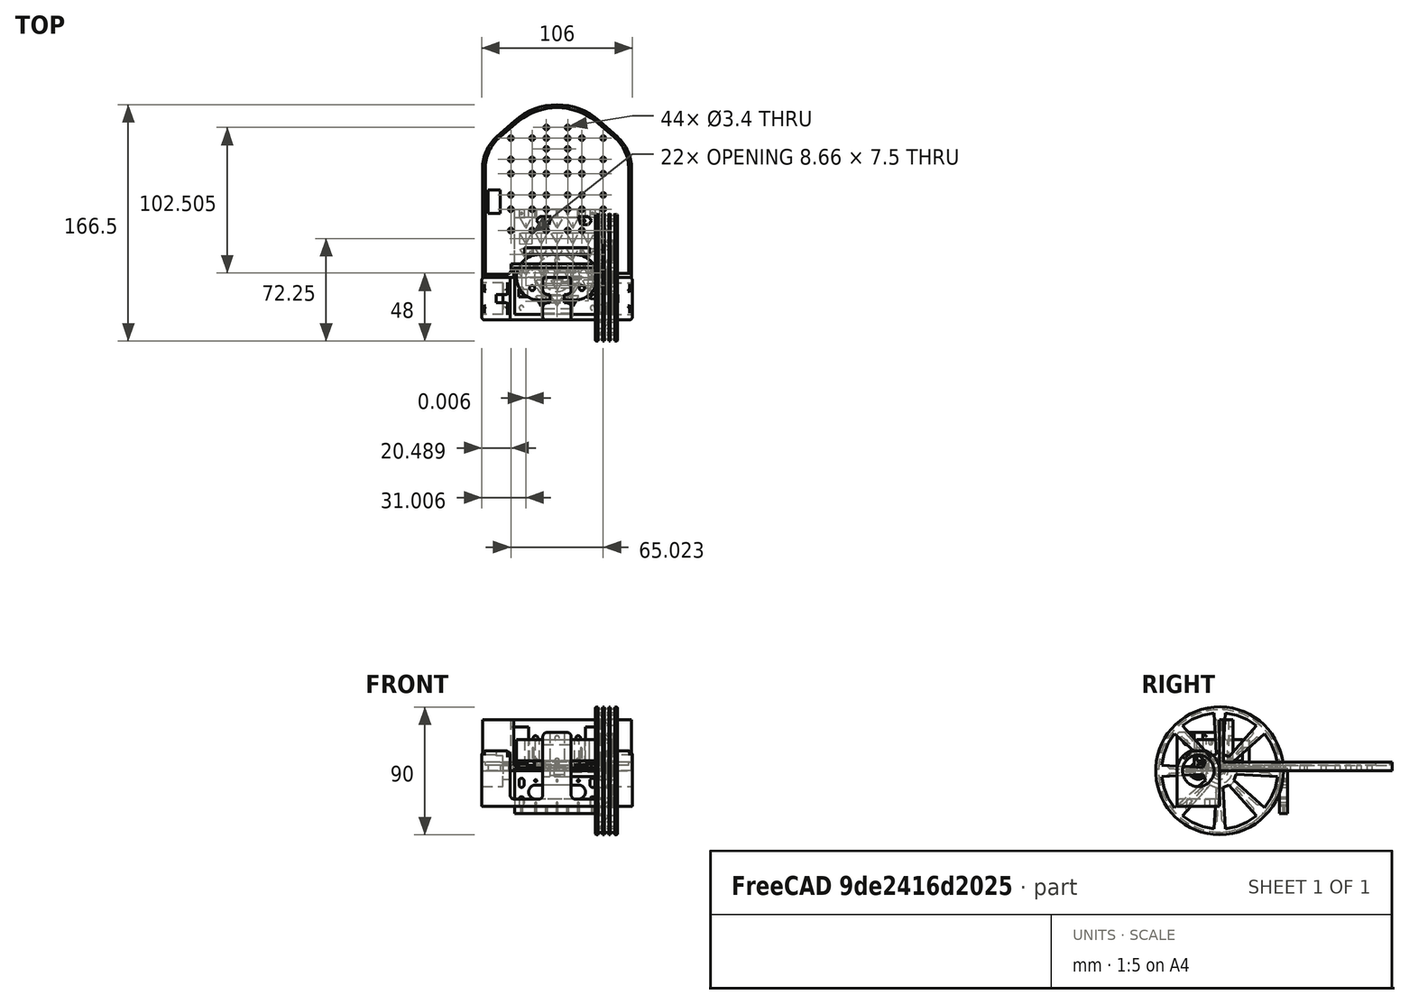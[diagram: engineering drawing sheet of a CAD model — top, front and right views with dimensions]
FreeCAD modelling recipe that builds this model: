
FCSTD DOCUMENT  (FreeCAD 0.19R24267 +99 (Git))
Label: MotoriGialliRuote90-r01
License: All rights reserved
LicenseURL: http://en.wikipedia.org/wiki/All_rights_reserved
objects: Sketcher::SketchObject×30, PartDesign::Pocket×18, PartDesign::Pad×11, PartDesign::Body×6, App::Part×6, PartDesign::Fillet×2, PartDesign::Revolution×1, PartDesign::FeatureBase×1, Mesh::Feature×1
note: 101 computed .brp shape members not serialized (recipe doc carries the construction recipe); baked Part::Feature solids carry a one-line shape summary decoded from their .brp

FEATURE [Sketcher::SketchObject] Sketch  label="ProfiloPrincipaleStaffa"
  FullyConstrained = false
  MapMode = 5
  Placement = pos=(0,0,0) rot=(1,0,0;1.5708rad)
  Support = -> [XZ_Plane001]
  constraints (76):
    c: Vertical(g1)
    c: Horizontal(g2)
    c: Coincident(g3,g4)
    c: Horizontal(g4)
    c: Horizontal(g5)
    c: Vertical(g6)
    c: Equal(g5,g2)
    c: Vertical(g3)
    c: DistanceY(g3,g-1) = 20
    c: Horizontal(g7)
    c: DistanceX(g7,g7) = 20
    c: DistanceX(g7,g3) = 43
    c: Tangent(g0,g8) = 1.5708
    c: Tangent(g1,g8) = 1.5708
    c: Tangent(g0,g9) = 1.5708
    c: Tangent(g6,g9) = 1.5708
    c: Equal(g9,g8)
    c: Radius(g9) = 3
    c: DistanceY(g-1,g0) = 27
    c: Tangent(g5,g10) = -1.5708
    c: Tangent(g6,g10) = -1.5708
    c: Tangent(g1,g11) = -1.5708
    c: Tangent(g2,g11) = -1.5708
    c: Equal(g11,g10)
    c: Equal(g10,g9)
    c: Coincident(g7,g6)
    c: Coincident(g7,g1)
    c: Coincident(g12,g5)
    c: PointOnObject(g12,g4)
    c: Vertical(g12)
    c: DistanceY(g12,g5) = 5
    c: Vertical(g13)
    c: Horizontal(g14)
    c: Coincident(g15,g3)
    c: Vertical(g15)
    c: Tangent(g2,g16) = -1.5708
    c: Tangent(g13,g16) = -1.5708
    c: Equal(g16,g11)
    c: Coincident(g17,g1)
    c: Coincident(g17,g13)
    c: DistanceX(g17,g17) = 23
    c: Symmetric(g0,g0,g-2)
    c: Tangent(g13,g18) = 1.5708
    c: Tangent(g14,g18) = 1.5708
    c: Tangent(g14,g19) = 1.5708
    c: Tangent(g15,g19) = 1.5708
    c: Equal(g19,g18)
    c: Equal(g18,g16)
    c: Coincident(g20,g13)
    c: Coincident(g20,g15)
    c: Vertical(g21)
    c: Horizontal(g22)
    c: Vertical(g23)
    c: Coincident(g23,g24)
    c: Vertical(g24)
    c: Coincident(g24,g4)
    c: Tangent(g23,g25) = -1.5708
    c: Tangent(g22,g25) = -1.5708
    c: Tangent(g22,g26) = -1.5708
    c: Tangent(g21,g26) = -1.5708
    c: Tangent(g21,g27) = 1.5708
    c: Tangent(g5,g27) = -1.5708
    c: Equal(g27,g26)
    c: Equal(g26,g25)
    c: Equal(g25,g10)
    c: Coincident(g28,g21)
    c: Coincident(g28,g13)
    c: Horizontal(g28)
    c: Equal(g14,g22)
    c: Coincident(g29,g23)
    c: Coincident(g29,g5)
    c: Horizontal(g29)
    c: Coincident(g30,g2)
    c: Coincident(g30,g3)
    c: Horizontal(g30)
    c: DistanceY(g-1,g14) = 14
FEATURE [PartDesign::Pad] Pad  label="ProfiloPrincipaleStaffa001"
  AllowMultiFace = false
  Direction = (1,1,1)
  Length = 30
  Length2 = 100
  Placement = pos=(0,0,0) rot=(1,0,0;1.5708rad)
  Profile = -> Sketch
  Type = 0
FEATURE [PartDesign::Pocket] Pocket  label="Unnamed001"
  AllowMultiFace = false
  Length = 100
  Length2 = 100
  Type = 0
FEATURE [Sketcher::SketchObject] Sketch002  label="Unnamed002"
  FullyConstrained = true
FEATURE [PartDesign::Pocket] Pocket001  label="Unnamed003"
  AllowMultiFace = false
  Length = 100
  Length2 = 100
  Type = 0
FEATURE [Sketcher::SketchObject] Sketch003  label="Unnamed004"
  FullyConstrained = true
FEATURE [PartDesign::Pocket] Pocket002  label="Unnamed005"
  AllowMultiFace = false
  Length = 100
  Length2 = 100
  Type = 0
FEATURE [Sketcher::SketchObject] Sketch001  label="ScontornoSupportoCuscinettiSX"
  FullyConstrained = false
  MapMode = 5
  Placement = pos=(-53,0,0) rot=(0.707107,0,-0.707107;3.14159rad)
  Support = -> [Pocket002]
  constraints (97):
    c: Coincident(g0,g1)
    c: Coincident(g11,g2)
    c: Coincident(g2,g3)
    c: Coincident(g10,g0)
    c: Horizontal(g0)
    c: Horizontal(g2)
    c: Vertical(g1)
    c: Vertical(g3)
    c: Horizontal(g4)
    c: Coincident(g4,g5)
    c: Vertical(g5)
    c: Coincident(g5,g6)
    c: Horizontal(g6)
    c: Horizontal(g7)
    c: Coincident(g7,g8)
    c: Vertical(g8)
    c: Coincident(g8,g9)
    c: Equal(g8,g5)
    c: DistanceY(g8,g7) = 6
    c: Tangent(g3,g10)
    c: Tangent(g1,g11)
    c: Horizontal(g9)
    c: Tangent(g7,g12) = 1.5708
    c: Tangent(g10,g12) = -1.5708
    c: Tangent(g9,g13) = 1.5708
    c: Tangent(g3,g13) = -1.5708
    c: Tangent(g11,g14) = -1.5708
    c: Tangent(g6,g14) = -1.5708
    c: Tangent(g4,g15) = -1.5708
    c: Tangent(g1,g15) = -1.5708
    c: Equal(g15,g12)
    c: Equal(g12,g13)
    c: Radius(g12) = 3
    c: Equal(g10,g11)
    c: Equal(g11,g3)
    c: Equal(g1,g10)
    c: DistanceX(g0,g4) = 5
    c: DistanceX(g7,g0) = 10
    c: DistanceX(g2,g2) = 23
    c: DistanceX(g5,g-1) = 5
    c: Coincident(g16,g1)
    c: Coincident(g17,g16)
    c: Coincident(g17,g11)
    c: Vertical(g17)
    c: Equal(g17,g16)
    c: DistanceY(g-1,g16) = 15
    c: Coincident(g18,g19)
    c: Coincident(g29,g20)
    c: Coincident(g20,g21)
    c: Coincident(g28,g18)
    c: Horizontal(g18)
    c: Horizontal(g20)
    c: Vertical(g19)
    c: Vertical(g21)
    c: Horizontal(g22)
    c: Coincident(g22,g23)
    c: Vertical(g23)
    c: Coincident(g23,g24)
    c: Horizontal(g24)
    c: Horizontal(g25)
    c: Coincident(g25,g26)
    c: Vertical(g26)
    c: Coincident(g26,g27)
    c: Equal(g26,g23)
    c: Tangent(g21,g28)
    c: Tangent(g19,g29)
    c: Horizontal(g27)
    c: Tangent(g25,g30) = 1.5708
    c: Tangent(g28,g30) = -1.5708
    c: Tangent(g27,g31) = 1.5708
    c: Tangent(g21,g31) = -1.5708
    c: Tangent(g29,g32) = -1.5708
    c: Tangent(g24,g32) = -1.5708
    c: Tangent(g22,g33) = -1.5708
    c: Tangent(g19,g33) = -1.5708
    c: Equal(g33,g30)
    c: Equal(g30,g31)
    c: Radius(g30) = 3
    c: Equal(g28,g29)
    c: Equal(g29,g21)
    c: Equal(g19,g28)
    c: Coincident(g34,g19)
    c: Coincident(g35,g34)
    c: Coincident(g35,g29)
    c: Vertical(g35)
    c: Equal(g35,g34)
    c: Equal(g26,g5)
    c: Equal(g20,g0)
    c: Equal(g21,g1)
    c: DistanceY(g2,g0) = 20
    c: Coincident(g36,g16)
    c: PointOnObject(g36,g-2)
    c: Horizontal(g36)
    c: Coincident(g37,g36)
    c: Coincident(g37,g34)
    c: Horizontal(g37)
    c: Equal(g36,g37)
FEATURE [Sketcher::SketchObject] Sketch004  label="Unnamed006"
  FullyConstrained = true
FEATURE [PartDesign::Pocket] Pocket003  label="StaffaMotori004"
  AllowMultiFace = false
  BaseFeature = -> Pocket002
  Length = 25
  Length2 = 100
  Placement = pos=(0,0,0) rot=(1,0,0;1.5708rad)
  Profile = -> Sketch004
  Type = 0
FEATURE [PartDesign::Fillet] Fillet  label="StaffaMotori005"
  Base = -> Pocket003 [Edge114,Edge123]
  BaseFeature = -> Pocket003
  Placement = pos=(0,0,0) rot=(1,0,0;1.5708rad)
  Radius = 2
  SupportTransform = false
FEATURE [PartDesign::Pocket] Pocket004  label="Unnamed007"
  AllowMultiFace = false
  Length = 100
  Length2 = 100
  Type = 0
FEATURE [Sketcher::SketchObject] Sketch005  label="ScassoSedeCuscinettiRuotaDX"
  FullyConstrained = false
  MapMode = 5
  Placement = pos=(53,0,0) rot=(0.707107,0,0.707107;3.14159rad)
  Support = -> [Pocket004]
  sketch-geometry (1):
    g0: Circle CenterX=0 CenterY=15 CenterZ=0 NormalX=0 NormalY=0 NormalZ=1 AngleXU=0 Radius=11.1
  constraints (3):
    c: PointOnObject(g0,g-2)
    c: Radius(g0) = 11.1
    c: DistanceY(g-1,g0) = 15
FEATURE [Sketcher::SketchObject] Sketch006  label="Unnamed008"
  FullyConstrained = true
FEATURE [PartDesign::Pocket] Pocket005  label="StaffaMotori007"
  AllowMultiFace = false
  BaseFeature = -> Pocket004
  Length = 15
  Length2 = 100
  Placement = pos=(0,0,0) rot=(1,0,0;1.5708rad)
  Profile = -> Sketch006
  Type = 0
FEATURE [PartDesign::Pocket] Pocket006  label="Unnamed009"
  AllowMultiFace = false
  Length = 100
  Length2 = 100
  Type = 0
FEATURE [Sketcher::SketchObject] Sketch007  label="ForoMozzoRuotaSX"
  FullyConstrained = false
  MapMode = 5
  Placement = pos=(-38,0,0) rot=(0.707107,0,-0.707107;3.14159rad)
  Support = -> [Pocket006]
  sketch-geometry (1):
    g0: Circle CenterX=0 CenterY=15 CenterZ=0 NormalX=0 NormalY=0 NormalZ=1 AngleXU=0 Radius=6
  constraints (3):
    c: PointOnObject(g0,g-2)
    c: Radius(g0) = 6
    c: DistanceY(g-1,g0) = 15
FEATURE [Sketcher::SketchObject] Sketch008  label="Unnamed010"
  FullyConstrained = true
FEATURE [PartDesign::Pocket] Pocket007  label="StaffaMotori009"
  AllowMultiFace = false
  BaseFeature = -> Pocket006
  Length = 10
  Length2 = 100
  Placement = pos=(0,0,0) rot=(1,0,0;1.5708rad)
  Profile = -> Sketch008
  Type = 0
FEATURE [PartDesign::Pocket] Pocket008  label="Unnamed011"
  AllowMultiFace = false
  Length = 100
  Length2 = 100
  Type = 0
FEATURE [Sketcher::SketchObject] Sketch009  label="ForiFissaggioStaffaMotori"
  FullyConstrained = false
  MapMode = 5
  Placement = pos=(0,-1.3e-14,-20) rot=(0,0,1;3.14159rad)
  Support = -> [Pocket008]
  sketch-geometry (4):
    g0: Circle CenterX=-20 CenterY=6.25 CenterZ=0 NormalX=0 NormalY=0 NormalZ=1 AngleXU=0 Radius=1.6
    g1: LineSegment StartX=-20 StartY=15 StartZ=0 EndX=-20 EndY=6.25 EndZ=0
    g2: Circle CenterX=25 CenterY=21.5 CenterZ=0 NormalX=0 NormalY=0 NormalZ=1 AngleXU=0 Radius=1.6
    g3: Circle CenterX=-25 CenterY=8.5 CenterZ=0 NormalX=0 NormalY=0 NormalZ=1 AngleXU=0 Radius=1.6
  constraints (11):
    c: Coincident(g2,g0)
    c: Vertical(g2)
    c: Coincident(g3,g2)
    c: Vertical(g3)
    c: Equal(g2,g3)
    c: DistanceY(g-1,g2) = 15
    c: Coincident(g1,g3)
    c: DistanceY(g1,g0) = 17.5
    c: Equal(g0,g1)
    c: Radius(g0) = 1.6
    c: DistanceX(g1,g-1) = 20
FEATURE [Sketcher::SketchObject] Sketch010  label="Unnamed012"
  FullyConstrained = true
FEATURE [PartDesign::Pocket] Pocket009  label="StaffaMotori011"
  AllowMultiFace = false
  BaseFeature = -> Pocket008
  Length = 7
  Length2 = 100
  Placement = pos=(0,0,0) rot=(1,0,0;1.5708rad)
  Profile = -> Sketch010
  Type = 0
FEATURE [PartDesign::Body] Body  label="StaffaMotori"
  Group = -> [Sketch,Pad,Sketch001,Pocket,Sketch002,Pocket001,Sketch003,Pocket002,Sketch004,Pocket003,Fillet,Sketch005,Pocket004,Sketch006,Pocket005,Sketch007,Pocket006,Sketch008,Pocket007,Sketch009,Pocket008,Sketch010,Pocket009]
  Origin = -> Origin001
  Tip = -> Pocket009
FEATURE [App::Part] Part  label="Staffa Motori"
  Group = -> [Body]
  Origin = -> Origin
  Placement = pos=(0,0,15) rot=(1,0,0;1.5708rad)
FEATURE [Sketcher::SketchObject] Sketch011  label="ProfiloCerchione90asse8"
  FullyConstrained = false
  MapMode = 5
  Placement = pos=(0,0,0) rot=(1,0,0;1.5708rad)
  Support = -> [XZ_Plane003]
  constraints (107):
    c: Vertical(g0)
    c: Coincident(g0,g1)
    c: Horizontal(g1)
    c: Coincident(g1,g2)
    c: Vertical(g2)
    c: Coincident(g2,g3)
    c: Horizontal(g3)
    c: Vertical(g4)
    c: Coincident(g5,g6)
    c: Vertical(g6)
    c: Vertical(g7)
    c: Coincident(g7,g8)
    c: Vertical(g9)
    c: Horizontal(g10)
    c: Coincident(g0,g10)
    c: Equal(g12,g13)
    c: Equal(g13,g11)
    c: Radius(g11) = 1.6
    c: Coincident(g14,g11)
    c: Coincident(g15,g12)
    c: Coincident(g16,g12)
    c: Coincident(g16,g13)
    c: Coincident(g17,g11)
    c: Horizontal(g14)
    c: Equal(g17,g14)
    c: Horizontal(g17)
    c: Coincident(g17,g13)
    c: Equal(g17,g16)
    c: Equal(g16,g15)
    c: Horizontal(g16)
    c: Horizontal(g15)
    c: Tangent(g6,g18) = -1.5708
    c: Tangent(g14,g18) = -1.5708
    c: Tangent(g7,g19) = -1.5708
    c: Tangent(g15,g19) = -1.5708
    c: Equal(g19,g18)
    c: Radius(g18) = 1
    c: Coincident(g20,g11)
    c: Coincident(g20,g11)
    c: Coincident(g21,g13)
    c: Coincident(g21,g13)
    c: Horizontal(g21)
    c: Coincident(g22,g12)
    c: Coincident(g22,g12)
    c: Horizontal(g22)
    c: Horizontal(g20)
    c: PointOnObject(g11,g20)
    c: PointOnObject(g13,g21)
    c: PointOnObject(g12,g22)
    c: Equal(g14,g15)
    c: DistanceX(g6,g11) = 2
    c: Equal(g6,g7)
    c: Coincident(g23,g5)
    c: Coincident(g23,g7)
    c: Horizontal(g24)
    c: Tangent(g4,g25) = 1.5708
    c: Tangent(g5,g25) = 1.5708
    c: Tangent(g9,g26) = 1.5708
    c: Tangent(g8,g26) = 1.5708
    c: Coincident(g24,g5)
    c: Coincident(g24,g8)
    c: Coincident(g27,g4)
    c: Coincident(g27,g9)
    c: Radius(g25) = 5
    c: DistanceY(g14,g5) = 2
    c: Coincident(g28,g25)
    c: Coincident(g28,g4)
    c: Coincident(g29,g9)
    c: Coincident(g29,g26)
    c: Coincident(g30,g26)
    c: Coincident(g30,g7)
    c: Vertical(g30)
    c: Coincident(g31,g25)
    c: Coincident(g31,g5)
    c: Equal(g28,g29)
    c: Equal(g31,g30)
    c: DistanceY(g15,g26) = 9
    c: PointOnObject(g32,g9)
    c: Horizontal(g32)
    c: Radius(g33) = 3
    c: Coincident(g10,g33)
    c: PointOnObject(g10,g-1)
    c: PointOnObject(g33,g-1)
    c: Coincident(g9,g33)
    c: Coincident(g34,g33)
    c: Coincident(g34,g9)
    c: Vertical(g34)
    c: Coincident(g35,g33)
    c: Coincident(g35,g10)
    c: DistanceY(g15,g-1) = 45
    c: Tangent(g3,g36) = 1.5708
    c: Tangent(g4,g36) = 1.5708
    c: Radius(g36) = 3
    c: DistanceY(g0,g0) = 4.1
    c: DistanceY(g2,g0) = 6
    c: DistanceX(g0,g2) = 29
    c: DistanceX(g3,g3) = 2
    c: Coincident(g32,g4)
    c: Coincident(g10,g37)
    c: PointOnObject(g37,g-1)
    c: Coincident(g37,g38)
    c: Coincident(g38,g7)
    c: Vertical(g38)
    c: DistanceX(g0,g-1) = 2
    c: Coincident(g39,g36)
    c: Coincident(g39,g25)
    c: Radius(g39) = 16
FEATURE [PartDesign::Revolution] Revolution  label="RuoteDa90asse009"
  AllowMultiFace = false
  Angle = 360
  Axis = (1,0,0)
  Base = (0,0,0)
  Placement = pos=(0,0,0) rot=(1,0,0;1.5708rad)
  Profile = -> Sketch011
  ReferenceAxis = -> Sketch011 [H_Axis]
  Reversed = true
FEATURE [Sketcher::SketchObject] Sketch013  label="AllegerimentoRuota"
  FullyConstrained = false
  MapMode = 5
  Placement = pos=(42.6,0,0) rot=(0.707107,0,0.707107;3.14159rad)
  Support = -> [Revolution]
  sketch-geometry (6):
    g0: ArcOfCircle CenterX=0 CenterY=-0.8 CenterZ=0 NormalX=0 NormalY=0 NormalZ=1 AngleXU=0 Radius=2.4 StartAngle=3.14159 EndAngle=6.28319
    g1: LineSegment StartX=2.4 StartY=0.8 StartZ=0 EndX=2.4 EndY=-0.8 EndZ=0
    g2: LineSegment StartX=0 StartY=0 StartZ=0 EndX=0 EndY=-0.8 EndZ=0
    g3: LineSegment StartX=11.7694 StartY=-2.34108 StartZ=0 EndX=11.7694 EndY=2.34108 EndZ=0
    g4: LineSegment StartX=9.97764 StartY=6.66684 StartZ=0 EndX=6.66684 EndY=9.97764 EndZ=0
    g5: LineSegment StartX=2.34108 StartY=11.7694 StartZ=0 EndX=-2.34108 EndY=11.7694 EndZ=0
  constraints (14):
    c: Tangent(g0,g3) = 1.5708
    c: Tangent(g0,g2) = -1.5708
    c: Tangent(g2,g1) = -1.5708
    c: Tangent(g3,g1) = 1.5708
    c: Vertical(g2)
    c: Equal(g0,g1)
    c: Radius(g0) = 2.4
    c: DistanceY(g1,g0) = 1.6
    c: Coincident(g4,g0)
    c: Vertical(g4)
    c: Coincident(g5,g4)
    c: Equal(g5,g4)
    c: Coincident(g5,g1)
    c: Coincident(g-1,g4)
FEATURE [Sketcher::SketchObject] Sketch017  label="Unnamed013"
  FullyConstrained = true
FEATURE [PartDesign::Pocket] Pocket014  label="RuoteDa90asse014"
  AllowMultiFace = false
  BaseFeature = -> Revolution
  Length = 15000
  Length2 = 100
  Placement = pos=(0,0,0) rot=(1,0,0;1.5708rad)
  Profile = -> Sketch017
  Type = 0
FEATURE [PartDesign::Fillet] Fillet001  label="RuoteDa90asse015"
  Base = -> Pocket014 [Edge19,Edge21,Edge23,Edge25,Edge17,Edge27,Edge29,Edge31,Edge33,Edge35,Edge37,Edge39,Edge41,Edge11,Edge13,Edge15,Edge14,Edge18,Edge22,Edge26,Edge30,Edge34,Edge38,Edge10]
  BaseFeature = -> Pocket014
  Placement = pos=(0,0,0) rot=(1,0,0;1.5708rad)
  Radius = 2
  SupportTransform = false
FEATURE [PartDesign::Pocket] Pocket015  label="RuoteDa90asse016"
  AllowMultiFace = false
  BaseFeature = -> Fillet001
  Length = 12
  Length2 = 100
  Placement = pos=(0,0,0) rot=(1,0,0;1.5708rad)
  Profile = -> Sketch013
  Type = 0
FEATURE [PartDesign::FeatureBase] Clone
  BaseFeature = -> Pocket015
  Placement = pos=(0,0,0) rot=(1,0,0;1.5708rad)
FEATURE [PartDesign::Body] Body002
  BaseFeature = -> Pocket015
  Group = -> [Clone]
  Origin = -> Origin004
  Tip = -> Clone
FEATURE [App::Part] Part002  label="Ruote da 90 asse 8DX"
  Group = -> [Body002]
  Origin = -> Origin005
  Placement = pos=(27,0,0) rot=(0,0,1;0rad)
FEATURE [Sketcher::SketchObject] Sketch018  label="PortaArduinoSopraMotori001"
  FullyConstrained = false
  MapMode = 5
  Support = -> [XY_Plane007]
  constraints (429):
    c: Coincident(g0,g1)
    c: Coincident(g1,g2)
    c: Coincident(g2,g3)
    c: Coincident(g3,g0)
    c: Horizontal(g2)
    c: Vertical(g1)
    c: Vertical(g3)
    c: Symmetric(g0,g0,g-2)
    c: DistanceX(g0,g0) = 60
    c: DistanceY(g1,g-1) = 26
    c: DistanceY(g1,g0) = 74
    c: Coincident(g4,g5)
    c: Coincident(g5,g6)
    c: Coincident(g6,g4)
    c: Equal(g4,g5)
    c: Equal(g4,g6)
    c: PointOnObject(g4,g7)
    c: PointOnObject(g5,g7)
    c: PointOnObject(g6,g7)
    c: Radius(g7) = 5
    c: Horizontal(g4)
    c: Coincident(g8,g9)
    c: Coincident(g9,g10)
    c: Coincident(g10,g8)
    c: Equal(g8,g9)
    c: Equal(g8,g10)
    c: PointOnObject(g8,g11)
    c: PointOnObject(g9,g11)
    c: PointOnObject(g10,g11)
    c: Equal(g7,g11) = 5
    c: Horizontal(g8)
    c: Coincident(g4,g12)
    c: Coincident(g8,g12)
    c: Distance(g12) = 11
    c: Angle(g12) = 0.000544822
    c: Coincident(g13,g14)
    c: Coincident(g14,g15)
    c: Coincident(g15,g13)
    c: Equal(g13,g14)
    c: Equal(g13,g15)
    c: PointOnObject(g13,g16)
    c: PointOnObject(g14,g16)
    c: PointOnObject(g15,g16)
    c: Equal(g7,g16) = 5
    c: Horizontal(g13)
    c: Coincident(g8,g17)
    c: Coincident(g13,g17)
    c: Equal(g12,g17)
    c: Parallel(g17,g12)
    c: Coincident(g18,g19)
    c: Coincident(g19,g20)
    c: Coincident(g20,g18)
    c: Equal(g18,g19)
    c: Equal(g18,g20)
    c: PointOnObject(g18,g21)
    c: PointOnObject(g19,g21)
    c: PointOnObject(g20,g21)
    c: Equal(g7,g21) = 5
    c: Horizontal(g18)
    c: Coincident(g13,g22)
    c: Coincident(g18,g22)
    c: Equal(g12,g22)
    c: Parallel(g22,g12)
    c: Coincident(g23,g24)
    c: Coincident(g24,g25)
    c: Coincident(g25,g23)
    c: Equal(g23,g24)
    c: Equal(g23,g25)
    c: PointOnObject(g23,g26)
    c: PointOnObject(g24,g26)
    c: PointOnObject(g25,g26)
    c: Equal(g7,g26) = 5
    c: Horizontal(g23)
    c: Coincident(g18,g27)
    c: Coincident(g23,g27)
    c: Equal(g12,g27)
    c: Parallel(g27,g12)
    c: Coincident(g28,g29)
    c: Coincident(g29,g30)
    c: Coincident(g30,g28)
    c: Equal(g28,g29)
    c: Equal(g28,g30)
    c: PointOnObject(g28,g31)
    c: PointOnObject(g29,g31)
    c: PointOnObject(g30,g31)
    c: Equal(g7,g31) = 5
    c: Horizontal(g28)
    c: Coincident(g4,g32)
    c: Coincident(g28,g32)
    c: Equal(g32,g12)
    c: Perpendicular(g32,g12)
    c: Coincident(g33,g34)
    c: Coincident(g34,g35)
    c: Coincident(g35,g33)
    c: Equal(g33,g34)
    c: Equal(g33,g35)
    c: PointOnObject(g33,g36)
    c: PointOnObject(g34,g36)
    c: PointOnObject(g35,g36)
    c: Equal(g7,g36) = 5
    c: Horizontal(g33)
    c: Coincident(g28,g37)
    c: Coincident(g33,g37)
    c: Equal(g12,g37)
    c: Parallel(g37,g12)
    c: Coincident(g38,g39)
    c: Coincident(g39,g40)
    c: Coincident(g40,g38)
    c: Equal(g38,g39)
    c: Equal(g38,g40)
    c: PointOnObject(g38,g41)
    c: PointOnObject(g39,g41)
    c: PointOnObject(g40,g41)
    c: Equal(g7,g41) = 5
    c: Horizontal(g38)
    c: Coincident(g33,g42)
    c: Coincident(g38,g42)
    c: Equal(g12,g42)
    c: Parallel(g42,g12)
    c: Coincident(g43,g44)
    c: Coincident(g44,g45)
    c: Coincident(g45,g43)
    c: Equal(g43,g44)
    c: Equal(g43,g45)
    c: PointOnObject(g43,g46)
    c: PointOnObject(g44,g46)
    c: PointOnObject(g45,g46)
    c: Equal(g7,g46) = 5
    c: Horizontal(g43)
    c: Coincident(g38,g47)
    c: Coincident(g43,g47)
    c: Equal(g12,g47)
    c: Parallel(g47,g12)
    c: Coincident(g48,g49)
    c: Coincident(g49,g50)
    c: Coincident(g50,g48)
    c: Equal(g48,g49)
    c: Equal(g48,g50)
    c: PointOnObject(g48,g51)
    c: PointOnObject(g49,g51)
    c: PointOnObject(g50,g51)
    c: Equal(g7,g51) = 5
    c: Horizontal(g48)
    c: Coincident(g43,g52)
    c: Coincident(g48,g52)
    c: Equal(g12,g52)
    c: Parallel(g52,g12)
    c: Coincident(g53,g54)
    c: Coincident(g54,g55)
    c: Coincident(g55,g53)
    c: Equal(g53,g54)
    c: Equal(g53,g55)
    c: PointOnObject(g53,g56)
    c: PointOnObject(g54,g56)
    c: PointOnObject(g55,g56)
    c: Equal(g7,g56) = 5
    c: Horizontal(g53)
    c: Coincident(g28,g57)
    c: Coincident(g53,g57)
    c: Equal(g32,g57)
    c: Perpendicular(g57,g12)
    c: Coincident(g58,g59)
    c: Coincident(g59,g60)
    c: Coincident(g60,g58)
    c: Equal(g58,g59)
    c: Equal(g58,g60)
    c: PointOnObject(g58,g61)
    c: PointOnObject(g59,g61)
    c: PointOnObject(g60,g61)
    c: Equal(g7,g61) = 5
    c: Horizontal(g58)
    c: Coincident(g53,g62)
    c: Coincident(g58,g62)
    c: Equal(g12,g62)
    c: Parallel(g62,g12)
    c: Coincident(g63,g64)
    c: Coincident(g64,g65)
    c: Coincident(g65,g63)
    c: Equal(g63,g64)
    c: Equal(g63,g65)
    c: PointOnObject(g63,g66)
    c: PointOnObject(g64,g66)
    c: PointOnObject(g65,g66)
    c: Equal(g7,g66) = 5
    c: Horizontal(g63)
    c: Coincident(g58,g67)
    c: Coincident(g63,g67)
    c: Equal(g12,g67)
    c: Parallel(g67,g12)
    c: Coincident(g68,g69)
    c: Coincident(g69,g70)
    c: Coincident(g70,g68)
    c: Equal(g68,g69)
    c: Equal(g68,g70)
    c: PointOnObject(g68,g71)
    c: PointOnObject(g69,g71)
    c: PointOnObject(g70,g71)
    c: Equal(g7,g71) = 5
    c: Horizontal(g68)
    c: Coincident(g63,g72)
    c: Coincident(g68,g72)
    c: Equal(g12,g72)
    c: Parallel(g72,g12)
    c: Coincident(g73,g74)
    c: Coincident(g74,g75)
    c: Coincident(g75,g73)
    c: Equal(g73,g74)
    c: Equal(g73,g75)
    c: PointOnObject(g73,g76)
    c: PointOnObject(g74,g76)
    c: PointOnObject(g75,g76)
    c: Equal(g7,g76) = 5
    c: Horizontal(g73)
    c: Coincident(g68,g77)
    c: Coincident(g73,g77)
    c: Equal(g12,g77)
    c: Parallel(g77,g12)
    c: Coincident(g78,g79)
    c: Coincident(g79,g80)
    c: Coincident(g80,g78)
    c: Equal(g78,g79)
    c: Equal(g78,g80)
    c: PointOnObject(g78,g81)
    c: PointOnObject(g79,g81)
    c: PointOnObject(g80,g81)
    c: Equal(g7,g81) = 5
    c: Horizontal(g78)
    c: Coincident(g53,g82)
    c: Coincident(g78,g82)
    c: Equal(g32,g82)
    c: Perpendicular(g82,g12)
    c: Coincident(g83,g84)
    c: Coincident(g84,g85)
    c: Coincident(g85,g83)
    c: Equal(g83,g84)
    c: Equal(g83,g85)
    c: PointOnObject(g83,g86)
    c: PointOnObject(g84,g86)
    c: PointOnObject(g85,g86)
    c: Equal(g7,g86) = 5
    c: Horizontal(g83)
    c: Coincident(g78,g87)
    c: Coincident(g83,g87)
    c: Equal(g12,g87)
    c: Parallel(g87,g12)
    c: Coincident(g88,g89)
    c: Coincident(g89,g90)
    c: Coincident(g90,g88)
    c: Equal(g88,g89)
    c: Equal(g88,g90)
    c: PointOnObject(g88,g91)
    c: PointOnObject(g89,g91)
    c: PointOnObject(g90,g91)
    c: Equal(g7,g91) = 5
    c: Horizontal(g88)
    c: Coincident(g83,g92)
    c: Coincident(g88,g92)
    c: Equal(g12,g92)
    c: Parallel(g92,g12)
    c: Coincident(g93,g94)
    c: Coincident(g94,g95)
    c: Coincident(g95,g93)
    c: Equal(g93,g94)
    c: Equal(g93,g95)
    c: PointOnObject(g93,g96)
    c: PointOnObject(g94,g96)
    c: PointOnObject(g95,g96)
    c: Equal(g7,g96) = 5
    c: Horizontal(g93)
    c: Coincident(g88,g97)
    c: Coincident(g93,g97)
    c: Equal(g12,g97)
    c: Parallel(g97,g12)
    c: Coincident(g98,g99)
    c: Coincident(g99,g100)
    c: Coincident(g100,g98)
    c: Equal(g98,g99)
    c: Equal(g98,g100)
    c: PointOnObject(g98,g101)
    c: PointOnObject(g99,g101)
    c: PointOnObject(g100,g101)
    c: Equal(g7,g101) = 5
    c: Horizontal(g98)
    c: Coincident(g93,g102)
    c: Coincident(g98,g102)
    c: Equal(g12,g102)
    c: Parallel(g102,g12)
    c: Coincident(g103,g104)
    c: Coincident(g104,g105)
    c: Coincident(g105,g103)
    c: Equal(g103,g104)
    c: Equal(g103,g105)
    c: PointOnObject(g103,g106)
    c: PointOnObject(g104,g106)
    c: PointOnObject(g105,g106)
    c: Equal(g7,g106) = 5
    c: Horizontal(g103)
    c: Coincident(g78,g107)
    c: Coincident(g103,g107)
    c: Equal(g32,g107)
    c: Perpendicular(g107,g12)
    c: Coincident(g108,g109)
    c: Coincident(g109,g110)
    c: Coincident(g110,g108)
    c: Equal(g108,g109)
    c: Equal(g108,g110)
    c: PointOnObject(g108,g111)
    c: PointOnObject(g109,g111)
    c: PointOnObject(g110,g111)
    c: Equal(g7,g111) = 5
    c: Horizontal(g108)
    c: Coincident(g103,g112)
    c: Coincident(g108,g112)
    c: Equal(g12,g112)
    c: Parallel(g112,g12)
    c: Coincident(g113,g114)
    c: Coincident(g114,g115)
    c: Coincident(g115,g113)
    c: Equal(g113,g114)
    c: Equal(g113,g115)
    c: PointOnObject(g113,g116)
    c: PointOnObject(g114,g116)
    c: PointOnObject(g115,g116)
    c: Equal(g7,g116) = 5
    c: Horizontal(g113)
    c: Coincident(g108,g117)
    c: Coincident(g113,g117)
    c: Equal(g12,g117)
    c: Parallel(g117,g12)
    c: Coincident(g118,g119)
    c: Coincident(g119,g120)
    c: Coincident(g120,g118)
    c: Equal(g118,g119)
    c: Equal(g118,g120)
    c: PointOnObject(g118,g121)
    c: PointOnObject(g119,g121)
    c: PointOnObject(g120,g121)
    c: Equal(g7,g121) = 5
    c: Horizontal(g118)
    c: Coincident(g113,g122)
    c: Coincident(g118,g122)
    c: Equal(g12,g122)
    c: Parallel(g122,g12)
    c: Coincident(g123,g124)
    c: Coincident(g124,g125)
    c: Coincident(g125,g123)
    c: Equal(g123,g124)
    c: Equal(g123,g125)
    c: PointOnObject(g123,g126)
    c: PointOnObject(g124,g126)
    c: PointOnObject(g125,g126)
    c: Equal(g7,g126) = 5
    c: Horizontal(g123)
    c: Coincident(g118,g127)
    c: Coincident(g123,g127)
    c: Equal(g12,g127)
    c: Parallel(g127,g12)
    c: Coincident(g128,g129)
    c: Coincident(g129,g130)
    c: Coincident(g130,g128)
    c: Equal(g128,g129)
    c: Equal(g128,g130)
    c: PointOnObject(g128,g131)
    c: PointOnObject(g129,g131)
    c: PointOnObject(g130,g131)
    c: Equal(g7,g131) = 5
    c: Horizontal(g128)
    c: Coincident(g103,g132)
    c: Coincident(g128,g132)
    c: Equal(g32,g132)
    c: Perpendicular(g132,g12)
    c: Coincident(g133,g134)
    c: Coincident(g134,g135)
    c: Coincident(g135,g133)
    c: Equal(g133,g134)
    c: Equal(g133,g135)
    c: PointOnObject(g133,g136)
    c: PointOnObject(g134,g136)
    c: PointOnObject(g135,g136)
    c: Equal(g7,g136) = 5
    c: Horizontal(g133)
    c: Coincident(g128,g137)
    c: Coincident(g133,g137)
    c: Equal(g12,g137)
    c: Parallel(g137,g12)
    c: Coincident(g138,g139)
    c: Coincident(g139,g140)
    c: Coincident(g140,g138)
    c: Equal(g138,g139)
    c: Equal(g138,g140)
    c: PointOnObject(g138,g141)
    c: PointOnObject(g139,g141)
    c: PointOnObject(g140,g141)
    c: Equal(g7,g141) = 5
    c: Horizontal(g138)
    c: Coincident(g133,g142)
    c: Coincident(g138,g142)
    c: Equal(g12,g142)
    c: Parallel(g142,g12)
    c: Coincident(g143,g144)
    c: Coincident(g144,g145)
    c: Coincident(g145,g143)
    c: Equal(g143,g144)
    c: Equal(g143,g145)
    c: PointOnObject(g143,g146)
    c: PointOnObject(g144,g146)
    c: PointOnObject(g145,g146)
    c: Equal(g7,g146) = 5
    c: Horizontal(g143)
    c: Coincident(g138,g147)
    c: Coincident(g143,g147)
    c: Equal(g12,g147)
    c: Parallel(g147,g12)
    c: Coincident(g148,g149)
    c: Coincident(g149,g150)
    c: Coincident(g150,g148)
    c: Equal(g148,g149)
    c: Equal(g148,g150)
    c: PointOnObject(g148,g151)
    c: PointOnObject(g149,g151)
    c: PointOnObject(g150,g151)
    c: Equal(g7,g151) = 5
    c: Horizontal(g148)
    c: Coincident(g143,g152)
    c: Coincident(g148,g152)
    c: Equal(g12,g152)
    c: Parallel(g152,g12)
    c: PointOnObject(g14,g-2)
    c: DistanceY(g4,g0) = 6
FEATURE [Mesh::Feature] Arduino_ipt  label="Arduino.ipt"
  Placement = pos=(35,0,38) rot=(0,0,1;0rad)
FEATURE [PartDesign::Pad] Pad001  label="PortaArduinoSopraMotori002"
  AllowMultiFace = false
  Direction = (1,1,1)
  Length = 2
  Length2 = 100
  Profile = -> Sketch018
  Type = 0
FEATURE [PartDesign::Pad] Pad002  label="Unnamed014"
  AllowMultiFace = false
  Direction = (1,1,1)
  Length = 100
  Length2 = 100
  Type = 0
FEATURE [Sketcher::SketchObject] Sketch020  label="Unnamed015"
  FullyConstrained = true
FEATURE [PartDesign::Pad] Pad003  label="Unnamed016"
  AllowMultiFace = false
  Direction = (1,1,1)
  Length = 100
  Length2 = 100
  Type = 0
FEATURE [Sketcher::SketchObject] Sketch019  label="ForiSupportoMotoriPiuStaffaTimone"
  FullyConstrained = false
  MapMode = 5
  Placement = pos=(0,48,0) rot=(0,0.707107,0.707107;3.14159rad)
  Support = -> [Pad003]
  constraints (94):
    c: Vertical(g0)
    c: Vertical(g1)
    c: Coincident(g2,g3)
    c: Horizontal(g3)
    c: Coincident(g3,g4)
    c: Horizontal(g5)
    c: Coincident(g6,g7)
    c: Horizontal(g7)
    c: Coincident(g23,g2)
    c: Coincident(g1,g7)
    c: Coincident(g8,g0)
    c: Coincident(g8,g24)
    c: Coincident(g3,g9)
    c: Coincident(g9,g10)
    c: Horizontal(g10)
    c: Coincident(g10,g11)
    c: Coincident(g11,g12)
    c: PointOnObject(g12,g5)
    c: Coincident(g12,g13)
    c: Coincident(g13,g14)
    c: Horizontal(g14)
    c: Coincident(g14,g15)
    c: Coincident(g15,g6)
    c: Horizontal(g16)
    c: Coincident(g16,g17)
    c: Vertical(g17)
    c: Coincident(g17,g18)
    c: Horizontal(g19)
    c: Coincident(g19,g20)
    c: Vertical(g20)
    c: Coincident(g20,g21)
    c: Coincident(g21,g22)
    c: Coincident(g5,g11)
    c: PointOnObject(g5,g13)
    c: Coincident(g0,g18)
    c: Coincident(g23,g16)
    c: Tangent(g0,g23)
    c: Coincident(g1,g19)
    c: Coincident(g24,g22)
    c: Tangent(g1,g24)
    c: Coincident(g25,g4)
    c: Coincident(g25,g5)
    c: Horizontal(g25)
    c: Coincident(g26,g5)
    c: Coincident(g26,g6)
    c: Horizontal(g26)
    c: Coincident(g27,g16)
    c: Coincident(g27,g0)
    c: Coincident(g28,g1)
    c: Coincident(g28,g22)
    c: Horizontal(g18)
    c: DistanceX(g4,g6) = 34
    c: DistanceX(g5,g5) = 19
    c: DistanceX(g25,g25) = 8
    c: DistanceX(g4,g-1) = 12
    c: Coincident(g29,g4)
    c: Coincident(g29,g9)
    c: Vertical(g29)
    c: Coincident(g30,g6)
    c: Coincident(g30,g14)
    c: Vertical(g30)
    c: Coincident(g31,g10)
    c: Horizontal(g31)
    c: Coincident(g32,g31)
    c: Horizontal(g32)
    c: Coincident(g33,g32)
    c: Coincident(g33,g13)
    c: Horizontal(g33)
    c: Coincident(g34,g5)
    c: Coincident(g34,g31)
    c: Vertical(g34)
    c: Coincident(g35,g5)
    c: Coincident(g35,g32)
    c: Vertical(g35)
    c: DistanceX(g10,g13) = 22.5
    c: Equal(g31,g33)
    c: DistanceX(g3,g4) = 2.5
    c: DistanceX(g6,g7) = 2.5
    c: DistanceX(g0,g8) = 54
    c: Symmetric(g0,g8,g-2)
    c: Equal(g36,g37)
    c: Equal(g37,g39)
    c: Equal(g39,g38)
    c: Radius(g38) = 0.75
    c: Coincident(g40,g36)
    c: Coincident(g40,g37)
    c: Horizontal(g40)
    c: DistanceX(g40,g40) = 27.75
    c: DistanceX(g36,g-1) = 8.75
    c: DistanceY(g36,g2) = 0.5
    c: DistanceX(g0,g38) = 3
    c: DistanceY(g38,g-1) = 11
    c: DistanceX(g39,g1) = 2.75
    c: DistanceY(g39,g-1) = 12.25
FEATURE [Sketcher::SketchObject] Sketch021  label="Unnamed017"
  FullyConstrained = true
FEATURE [PartDesign::Pocket] Pocket016  label="PortaArduinoSopraMotori005"
  AllowMultiFace = false
  BaseFeature = -> Pad003
  Length = 7
  Length2 = 100
  Profile = -> Sketch021
  Type = 0
FEATURE [Sketcher::SketchObject] Sketch022  label="ForiFissaggioTimone"
  FullyConstrained = false
  MapMode = 5
  Placement = pos=(0,0,-30) rot=(1,0,0;3.14159rad)
  Support = -> [Pocket016]
  constraints (30):
    c: Horizontal(g0)
    c: Coincident(g1,g0)
    c: Horizontal(g1)
    c: Coincident(g2,g1)
    c: Coincident(g3,g2)
    c: Horizontal(g3)
    c: Coincident(g4,g3)
    c: Horizontal(g4)
    c: Coincident(g5,g0)
    c: Coincident(g6,g0)
    c: Coincident(g7,g1)
    c: PointOnObject(g8,g-2)
    c: Coincident(g9,g2)
    c: Coincident(g10,g3)
    c: Coincident(g11,g4)
    c: PointOnObject(g8,g2)
    c: Equal(g10,g9)
    c: Equal(g9,g11)
    c: Equal(g11,g8)
    c: Equal(g8,g7)
    c: Equal(g7,g6)
    c: Equal(g6,g5)
    c: Radius(g5) = 0.75
    c: Symmetric(g7,g9,g-2)
    c: Equal(g1,g3)
    c: Equal(g0,g4)
    c: DistanceY(g5,g-1) = 45
    c: DistanceX(g5,g-1) = 25
    c: DistanceX(g-1,g10) = 15
    c: DistanceX(g-1,g9) = 7.5
FEATURE [PartDesign::Pocket] Pocket017  label="PortaArduinoSopraMotori006"
  AllowMultiFace = false
  BaseFeature = -> Pocket016
  Length = 5
  Length2 = 100
  Profile = -> Sketch022
  Type = 0
FEATURE [PartDesign::Body] Body003  label="PortaArduinoSopraMotori"
  Group = -> [Sketch018,Pad001,Sketch019,Pad002,Sketch020,Pad003,Sketch021,Pocket016,Sketch022,Pocket017]
  Origin = -> Origin007
  Tip = -> Pocket017
FEATURE [App::Part] Part003  label="Porta Arduino Sopra Motori"
  Group = -> [Body003,Arduino_ipt]
  Origin = -> Origin006
  Placement = pos=(0,-17,15) rot=(0,0,1;0rad)
FEATURE [Sketcher::SketchObject] Sketch023  label="TimonePortaBatterie002"
  FullyConstrained = false
  MapMode = 5
  Support = -> [XY_Plane009]
  sketch-geometry (114):
    g0: LineSegment StartX=-52.5 StartY=0 StartZ=0 EndX=-30.5 EndY=0 EndZ=0
    g1: LineSegment StartX=-30.5 StartY=0 StartZ=0 EndX=-30.5 EndY=6.5 EndZ=0
    g2: LineSegment StartX=-30.5 StartY=6.5 StartZ=0 EndX=30.5 EndY=6.5 EndZ=0
    g3: LineSegment StartX=30.5 StartY=6.5 StartZ=0 EndX=30.5 EndY=0 EndZ=0
    g4: LineSegment StartX=30.5 StartY=0 StartZ=0 EndX=52.5 EndY=0 EndZ=0
    g5: LineSegment StartX=52.5 StartY=0 StartZ=0 EndX=52.5 EndY=76.5 EndZ=0
    g6: LineSegment StartX=42.5 StartY=98.8607 StartZ=0 EndX=30 EndY=110.041 EndZ=0
    g7: LineSegment StartX=-30 StartY=110.041 StartZ=0 EndX=-42.5 EndY=98.8607 EndZ=0
    g8: LineSegment StartX=-52.5 StartY=76.5 StartZ=0 EndX=-52.5 EndY=0 EndZ=0
    g9: ArcOfCircle CenterX=0 CenterY=76.5 CenterZ=0 NormalX=0 NormalY=0 NormalZ=1 AngleXU=0 Radius=45 StartAngle=0.841069 EndAngle=2.30052
    g10: LineSegment StartX=-30 StartY=110.041 StartZ=0 EndX=30 EndY=110.041 EndZ=0
    g11: ArcOfCircle CenterX=-22.5 CenterY=76.5 CenterZ=0 NormalX=0 NormalY=0 NormalZ=1 AngleXU=0 Radius=30 StartAngle=2.30052 EndAngle=3.14159
    g12: ArcOfCircle CenterX=22.5 CenterY=76.5 CenterZ=0 NormalX=0 NormalY=0 NormalZ=1 AngleXU=0 Radius=30 StartAngle=0 EndAngle=0.841069
    g13: LineSegment StartX=-52.5 StartY=76.5 StartZ=0 EndX=52.5 EndY=76.5 EndZ=0
    g14: LineSegment StartX=-42.5 StartY=98.8607 StartZ=0 EndX=42.5 EndY=98.8607 EndZ=0
    g15: LineSegment StartX=-52.5 StartY=76.5 StartZ=0 EndX=-52.5 EndY=121.5 EndZ=0
    g16: LineSegment StartX=-52.5 StartY=121.5 StartZ=0 EndX=52.5 EndY=121.5 EndZ=0
    g17: LineSegment StartX=52.5 StartY=121.5 StartZ=0 EndX=52.5 EndY=76.5 EndZ=0
    g18: Circle CenterX=17.5115 CenterY=32.9821 CenterZ=0 NormalX=0 NormalY=0 NormalZ=1 AngleXU=0 Radius=1.7
    g19: Circle CenterX=17.5115 CenterY=47.9821 CenterZ=0 NormalX=0 NormalY=0 NormalZ=1 AngleXU=0 Radius=1.7
    g20: Circle CenterX=32.5115 CenterY=47.9821 CenterZ=0 NormalX=0 NormalY=0 NormalZ=1 AngleXU=0 Radius=1.7
    g21: Circle CenterX=32.5115 CenterY=32.9821 CenterZ=0 NormalX=0 NormalY=0 NormalZ=1 AngleXU=0 Radius=1.7
    g22: LineSegment StartX=17.5115 StartY=47.9821 StartZ=0 EndX=32.5115 EndY=47.9821 EndZ=0
    g23: LineSegment StartX=32.5115 StartY=47.9821 StartZ=0 EndX=32.5115 EndY=32.9821 EndZ=0
    g24: LineSegment StartX=32.5115 StartY=32.9821 StartZ=0 EndX=17.5115 EndY=32.9821 EndZ=0
    g25: LineSegment StartX=17.5115 StartY=32.9821 StartZ=0 EndX=17.5115 EndY=47.9821 EndZ=0
    g26: Circle CenterX=-7.5 CenterY=32.9821 CenterZ=0 NormalX=0 NormalY=0 NormalZ=1 AngleXU=0 Radius=1.7
    g27: Circle CenterX=-7.5 CenterY=47.9821 CenterZ=0 NormalX=0 NormalY=0 NormalZ=1 AngleXU=0 Radius=1.7
    g28: Circle CenterX=7.5 CenterY=47.9821 CenterZ=0 NormalX=0 NormalY=0 NormalZ=1 AngleXU=0 Radius=1.7
    g29: Circle CenterX=7.5 CenterY=32.9821 CenterZ=0 NormalX=0 NormalY=0 NormalZ=1 AngleXU=0 Radius=1.7
    g30: LineSegment StartX=-7.5 StartY=47.9821 StartZ=0 EndX=7.5 EndY=47.9821 EndZ=0
    g31: LineSegment StartX=7.5 StartY=47.9821 StartZ=0 EndX=7.5 EndY=32.9821 EndZ=0
    g32: LineSegment StartX=7.5 StartY=32.9821 StartZ=0 EndX=-7.5 EndY=32.9821 EndZ=0
    g33: LineSegment StartX=-7.5 StartY=32.9821 StartZ=0 EndX=-7.5 EndY=47.9821 EndZ=0
    g34: LineSegment StartX=17.5115 StartY=32.9821 StartZ=0 EndX=-7.5 EndY=32.9821 EndZ=0
    g35: Circle CenterX=-32.5115 CenterY=32.9821 CenterZ=0 NormalX=0 NormalY=0 NormalZ=1 AngleXU=0 Radius=1.7
    g36: Circle CenterX=-32.5115 CenterY=47.9821 CenterZ=0 NormalX=0 NormalY=0 NormalZ=1 AngleXU=0 Radius=1.7
    g37: Circle CenterX=-17.5115 CenterY=47.9821 CenterZ=0 NormalX=0 NormalY=0 NormalZ=1 AngleXU=0 Radius=1.7
    g38: Circle CenterX=-17.5115 CenterY=32.9821 CenterZ=0 NormalX=0 NormalY=0 NormalZ=1 AngleXU=0 Radius=1.7
    g39: LineSegment StartX=-32.5115 StartY=47.9821 StartZ=0 EndX=-17.5115 EndY=47.9821 EndZ=0
    g40: LineSegment StartX=-17.5115 StartY=47.9821 StartZ=0 EndX=-17.5115 EndY=32.9821 EndZ=0
    g41: LineSegment StartX=-17.5115 StartY=32.9821 StartZ=0 EndX=-32.5115 EndY=32.9821 EndZ=0
    g42: LineSegment StartX=-32.5115 StartY=32.9821 StartZ=0 EndX=-32.5115 EndY=47.9821 EndZ=0
    g43: LineSegment StartX=-7.5 StartY=32.9821 StartZ=0 EndX=-32.5115 EndY=32.9821 EndZ=0
    g44: Circle CenterX=17.5115 CenterY=57.9936 CenterZ=0 NormalX=0 NormalY=0 NormalZ=1 AngleXU=0 Radius=1.7
    g45: Circle CenterX=17.5115 CenterY=72.9936 CenterZ=0 NormalX=0 NormalY=0 NormalZ=1 AngleXU=0 Radius=1.7
    g46: Circle CenterX=32.5115 CenterY=72.9936 CenterZ=0 NormalX=0 NormalY=0 NormalZ=1 AngleXU=0 Radius=1.7
    g47: Circle CenterX=32.5115 CenterY=57.9936 CenterZ=0 NormalX=0 NormalY=0 NormalZ=1 AngleXU=0 Radius=1.7
    g48: LineSegment StartX=17.5115 StartY=72.9936 StartZ=0 EndX=32.5115 EndY=72.9936 EndZ=0
    g49: LineSegment StartX=32.5115 StartY=72.9936 StartZ=0 EndX=32.5115 EndY=57.9936 EndZ=0
    g50: LineSegment StartX=32.5115 StartY=57.9936 StartZ=0 EndX=17.5115 EndY=57.9936 EndZ=0
    g51: LineSegment StartX=17.5115 StartY=57.9936 StartZ=0 EndX=17.5115 EndY=72.9936 EndZ=0
    g52: LineSegment StartX=17.5115 StartY=32.9821 StartZ=0 EndX=17.5115 EndY=57.9936 EndZ=0
    g53: Circle CenterX=-7.5 CenterY=57.9936 CenterZ=0 NormalX=0 NormalY=0 NormalZ=1 AngleXU=0 Radius=1.7
    g54: Circle CenterX=-7.5 CenterY=72.9936 CenterZ=0 NormalX=0 NormalY=0 NormalZ=1 AngleXU=0 Radius=1.7
    g55: Circle CenterX=7.5 CenterY=72.9936 CenterZ=0 NormalX=0 NormalY=0 NormalZ=1 AngleXU=0 Radius=1.7
    g56: Circle CenterX=7.5 CenterY=57.9936 CenterZ=0 NormalX=0 NormalY=0 NormalZ=1 AngleXU=0 Radius=1.7
    g57: LineSegment StartX=-7.5 StartY=72.9936 StartZ=0 EndX=7.5 EndY=72.9936 EndZ=0
    g58: LineSegment StartX=7.5 StartY=72.9936 StartZ=0 EndX=7.5 EndY=57.9936 EndZ=0
    g59: LineSegment StartX=7.5 StartY=57.9936 StartZ=0 EndX=-7.5 EndY=57.9936 EndZ=0
    g60: LineSegment StartX=-7.5 StartY=57.9936 StartZ=0 EndX=-7.5 EndY=72.9936 EndZ=0
    g61: LineSegment StartX=17.5115 StartY=57.9936 StartZ=0 EndX=-7.5 EndY=57.9936 EndZ=0
    g62: Circle CenterX=-32.5115 CenterY=57.9936 CenterZ=0 NormalX=0 NormalY=0 NormalZ=1 AngleXU=0 Radius=1.7
    g63: Circle CenterX=-32.5115 CenterY=72.9936 CenterZ=0 NormalX=0 NormalY=0 NormalZ=1 AngleXU=0 Radius=1.7
    g64: Circle CenterX=-17.5115 CenterY=72.9936 CenterZ=0 NormalX=0 NormalY=0 NormalZ=1 AngleXU=0 Radius=1.7
    g65: Circle CenterX=-17.5115 CenterY=57.9936 CenterZ=0 NormalX=0 NormalY=0 NormalZ=1 AngleXU=0 Radius=1.7
    g66: LineSegment StartX=-32.5115 StartY=72.9936 StartZ=0 EndX=-17.5115 EndY=72.9936 EndZ=0
    g67: LineSegment StartX=-17.5115 StartY=72.9936 StartZ=0 EndX=-17.5115 EndY=57.9936 EndZ=0
    g68: LineSegment StartX=-17.5115 StartY=57.9936 StartZ=0 EndX=-32.5115 EndY=57.9936 EndZ=0
    g69: LineSegment StartX=-32.5115 StartY=57.9936 StartZ=0 EndX=-32.5115 EndY=72.9936 EndZ=0
    g70: LineSegment StartX=-7.5 StartY=57.9936 StartZ=0 EndX=-32.5115 EndY=57.9936 EndZ=0
    g71: Circle CenterX=17.5115 CenterY=83.0051 CenterZ=0 NormalX=0 NormalY=0 NormalZ=1 AngleXU=0 Radius=1.7
    g72: Circle CenterX=17.5115 CenterY=98.0051 CenterZ=0 NormalX=0 NormalY=0 NormalZ=1 AngleXU=0 Radius=1.7
    g73: Circle CenterX=32.5115 CenterY=98.0051 CenterZ=0 NormalX=0 NormalY=0 NormalZ=1 AngleXU=0 Radius=1.7
    g74: Circle CenterX=32.5115 CenterY=83.0051 CenterZ=0 NormalX=0 NormalY=0 NormalZ=1 AngleXU=0 Radius=1.7
    g75: LineSegment StartX=17.5115 StartY=98.0051 StartZ=0 EndX=32.5115 EndY=98.0051 EndZ=0
    g76: LineSegment StartX=32.5115 StartY=98.0051 StartZ=0 EndX=32.5115 EndY=83.0051 EndZ=0
    g77: LineSegment StartX=32.5115 StartY=83.0051 StartZ=0 EndX=17.5115 EndY=83.0051 EndZ=0
    g78: LineSegment StartX=17.5115 StartY=83.0051 StartZ=0 EndX=17.5115 EndY=98.0051 EndZ=0
    g79: LineSegment StartX=17.5115 StartY=57.9936 StartZ=0 EndX=17.5115 EndY=83.0051 EndZ=0
    g80: Circle CenterX=-7.5 CenterY=83.0051 CenterZ=0 NormalX=0 NormalY=0 NormalZ=1 AngleXU=0 Radius=1.7
    g81: Circle CenterX=-7.5 CenterY=98.0051 CenterZ=0 NormalX=0 NormalY=0 NormalZ=1 AngleXU=0 Radius=1.7
    g82: Circle CenterX=7.5 CenterY=98.0051 CenterZ=0 NormalX=0 NormalY=0 NormalZ=1 AngleXU=0 Radius=1.7
    g83: Circle CenterX=7.5 CenterY=83.0051 CenterZ=0 NormalX=0 NormalY=0 NormalZ=1 AngleXU=0 Radius=1.7
    g84: LineSegment StartX=-7.5 StartY=98.0051 StartZ=0 EndX=7.5 EndY=98.0051 EndZ=0
    g85: LineSegment StartX=7.5 StartY=98.0051 StartZ=0 EndX=7.5 EndY=83.0051 EndZ=0
    g86: LineSegment StartX=7.5 StartY=83.0051 StartZ=0 EndX=-7.5 EndY=83.0051 EndZ=0
    g87: LineSegment StartX=-7.5 StartY=83.0051 StartZ=0 EndX=-7.5 EndY=98.0051 EndZ=0
    g88: LineSegment StartX=17.5115 StartY=83.0051 StartZ=0 EndX=-7.5 EndY=83.0051 EndZ=0
    g89: Circle CenterX=-32.5115 CenterY=83.0051 CenterZ=0 NormalX=0 NormalY=0 NormalZ=1 AngleXU=0 Radius=1.7
    g90: Circle CenterX=-32.5115 CenterY=98.0051 CenterZ=0 NormalX=0 NormalY=0 NormalZ=1 AngleXU=0 Radius=1.7
    g91: Circle CenterX=-17.5115 CenterY=98.0051 CenterZ=0 NormalX=0 NormalY=0 NormalZ=1 AngleXU=0 Radius=1.7
    g92: Circle CenterX=-17.5115 CenterY=83.0051 CenterZ=0 NormalX=0 NormalY=0 NormalZ=1 AngleXU=0 Radius=1.7
    g93: LineSegment StartX=-32.5115 StartY=98.0051 StartZ=0 EndX=-17.5115 EndY=98.0051 EndZ=0
    g94: LineSegment StartX=-17.5115 StartY=98.0051 StartZ=0 EndX=-17.5115 EndY=83.0051 EndZ=0
    g95: LineSegment StartX=-17.5115 StartY=83.0051 StartZ=0 EndX=-32.5115 EndY=83.0051 EndZ=0
    g96: LineSegment StartX=-32.5115 StartY=83.0051 StartZ=0 EndX=-32.5115 EndY=98.0051 EndZ=0
    g97: LineSegment StartX=-7.5 StartY=83.0051 StartZ=0 EndX=-32.5115 EndY=83.0051 EndZ=0
    g98: Circle CenterX=-7.5 CenterY=90.5051 CenterZ=0 NormalX=0 NormalY=0 NormalZ=1 AngleXU=0 Radius=1.7
    g99: Circle CenterX=-7.5 CenterY=105.505 CenterZ=0 NormalX=0 NormalY=0 NormalZ=1 AngleXU=0 Radius=1.7
    g100: Circle CenterX=7.5 CenterY=105.505 CenterZ=0 NormalX=0 NormalY=0 NormalZ=1 AngleXU=0 Radius=1.7
    g101: Circle CenterX=7.5 CenterY=90.5051 CenterZ=0 NormalX=0 NormalY=0 NormalZ=1 AngleXU=0 Radius=1.7
    g102: LineSegment StartX=-7.5 StartY=105.505 StartZ=0 EndX=7.5 EndY=105.505 EndZ=0
    g103: LineSegment StartX=7.5 StartY=105.505 StartZ=0 EndX=7.5 EndY=90.5051 EndZ=0
    g104: LineSegment StartX=7.5 StartY=90.5051 StartZ=0 EndX=-7.5 EndY=90.5051 EndZ=0
    g105: LineSegment StartX=-7.5 StartY=90.5051 StartZ=0 EndX=-7.5 EndY=105.505 EndZ=0
    g106: LineSegment StartX=-30.5 StartY=0 StartZ=0 EndX=30.5 EndY=0 EndZ=0
    g107: Circle CenterX=-24.8274 CenterY=3 CenterZ=0 NormalX=0 NormalY=0 NormalZ=1 AngleXU=0 Radius=1.7
    g108: Circle CenterX=-7.5 CenterY=3 CenterZ=0 NormalX=0 NormalY=0 NormalZ=1 AngleXU=0 Radius=1.7
    g109: Circle CenterX=7.5 CenterY=3 CenterZ=0 NormalX=0 NormalY=0 NormalZ=1 AngleXU=0 Radius=1.7
    g110: Circle CenterX=25.1726 CenterY=3 CenterZ=0 NormalX=0 NormalY=0 NormalZ=1 AngleXU=0 Radius=1.7
    g111: LineSegment StartX=-24.8274 StartY=3 StartZ=0 EndX=-7.5 EndY=3 EndZ=0
    g112: LineSegment StartX=-7.5 StartY=3 StartZ=0 EndX=7.5 EndY=3 EndZ=0
    g113: LineSegment StartX=7.5 StartY=3 StartZ=0 EndX=25.1726 EndY=3 EndZ=0
  constraints (276):
    c: Horizontal(g0)
    c: Coincident(g0,g1)
    c: Vertical(g1)
    c: Coincident(g1,g2)
    c: Coincident(g2,g3)
    c: Vertical(g3)
    c: Coincident(g3,g4)
    c: Horizontal(g4)
    c: Coincident(g4,g5)
    c: Vertical(g5)
    c: Coincident(g8,g0)
    c: Vertical(g8)
    c: PointOnObject(g9,g-2)
    c: Tangent(g9,g6) = -1.5708
    c: Coincident(g10,g7)
    c: Coincident(g10,g6)
    c: Horizontal(g10)
    c: Tangent(g7,g11) = -1.5708
    c: Tangent(g8,g11) = -1.5708
    c: Tangent(g6,g12) = -1.5708
    c: Tangent(g5,g12) = -1.5708
    c: Equal(g12,g11)
    c: Coincident(g13,g8)
    c: Coincident(g13,g5)
    c: Horizontal(g13)
    c: Coincident(g14,g7)
    c: Coincident(g14,g6)
    c: Tangent(g7,g9) = -1.5708
    c: PointOnObject(g0,g-1)
    c: PointOnObject(g4,g-1)
    c: DistanceY(g-1,g2) = 6.5
    c: DistanceX(g1,g2) = 61
    c: Symmetric(g1,g2,g-2)
    c: DistanceX(g0,g4) = 105
    c: DistanceY(g2,g5) = 70
    c: Radius(g9) = 45
    c: Radius(g11) = 30
    c: Coincident(g8,g15)
    c: Vertical(g15)
    c: Coincident(g15,g16)
    c: Horizontal(g16)
    c: Tangent(g16,g9)
    c: Coincident(g16,g17)
    c: Coincident(g17,g5)
    c: Vertical(g17)
    c: DistanceY(g5,g16) = 45
    c: Coincident(g22,g23)
    c: Coincident(g23,g24)
    c: Coincident(g24,g25)
    c: Coincident(g25,g22)
    c: Horizontal(g22)
    c: Horizontal(g24)
    c: Vertical(g23)
    c: Vertical(g25)
    c: Coincident(g22,g19)
    c: Coincident(g23,g21)
    c: Equal(g20,g19)
    c: Equal(g19,g18)
    c: Equal(g18,g21)
    c: Radius(g19) = 1.7
    c: Coincident(g18,g24)
    c: Coincident(g20,g22)
    c: Equal(g22,g25)
    c: DistanceY(g25,g25) = 15
    c: Coincident(g30,g31)
    c: Coincident(g31,g32)
    c: Coincident(g32,g33)
    c: Coincident(g33,g30)
    c: Horizontal(g30)
    c: Horizontal(g32)
    c: Vertical(g31)
    c: Vertical(g33)
    c: Coincident(g30,g27)
    c: Coincident(g31,g29)
    c: Equal(g28,g27)
    c: Equal(g27,g26)
    c: Equal(g26,g29)
    c: Equal(g19,g27) = 1.7
    c: Coincident(g26,g32)
    c: Coincident(g28,g30)
    c: Equal(g30,g33)
    c: Equal(g25,g33) = 15
    c: Coincident(g18,g34)
    c: Coincident(g26,g34)
    c: Distance(g34) = 25.0115
    c: Angle(g34) = 3.14159
    c: Coincident(g39,g40)
    c: Coincident(g40,g41)
    c: Coincident(g41,g42)
    c: Coincident(g42,g39)
    c: Horizontal(g39)
    c: Horizontal(g41)
    c: Vertical(g40)
    c: Vertical(g42)
    c: Coincident(g39,g36)
    c: Coincident(g40,g38)
    c: Equal(g37,g36)
    c: Equal(g36,g35)
    c: Equal(g35,g38)
    c: Equal(g19,g36) = 1.7
    c: Coincident(g35,g41)
    c: Coincident(g37,g39)
    c: Equal(g39,g42)
    c: Equal(g25,g42) = 15
    c: Coincident(g26,g43)
    c: Coincident(g35,g43)
    c: Equal(g34,g43)
    c: Parallel(g43,g34)
    c: Coincident(g48,g49)
    c: Coincident(g49,g50)
    c: Coincident(g50,g51)
    c: Coincident(g51,g48)
    c: Horizontal(g48)
    c: Horizontal(g50)
    c: Vertical(g49)
    c: Vertical(g51)
    c: Coincident(g48,g45)
    c: Coincident(g49,g47)
    c: Equal(g46,g45)
    c: Equal(g45,g44)
    c: Equal(g44,g47)
    c: Equal(g19,g45) = 1.7
    c: Coincident(g44,g50)
    c: Coincident(g46,g48)
    c: Equal(g48,g51)
    c: Equal(g25,g51) = 15
    c: Coincident(g18,g52)
    c: Coincident(g44,g52)
    c: Equal(g52,g34)
    c: Perpendicular(g52,g34)
    c: Coincident(g57,g58)
    c: Coincident(g58,g59)
    c: Coincident(g59,g60)
    c: Coincident(g60,g57)
    c: Horizontal(g57)
    c: Horizontal(g59)
    c: Vertical(g58)
    c: Vertical(g60)
    c: Coincident(g57,g54)
    c: Coincident(g58,g56)
    c: Equal(g55,g54)
    c: Equal(g54,g53)
    c: Equal(g53,g56)
    c: Equal(g19,g54) = 1.7
    c: Coincident(g53,g59)
    c: Coincident(g55,g57)
    c: Equal(g57,g60)
    c: Equal(g25,g60) = 15
    c: Coincident(g44,g61)
    c: Coincident(g53,g61)
    c: Equal(g34,g61)
    c: Parallel(g61,g34)
    c: Coincident(g66,g67)
    c: Coincident(g67,g68)
    c: Coincident(g68,g69)
    c: Coincident(g69,g66)
    c: Horizontal(g66)
    c: Horizontal(g68)
    c: Vertical(g67)
    c: Vertical(g69)
    c: Coincident(g66,g63)
    c: Coincident(g67,g65)
    c: Equal(g64,g63)
    c: Equal(g63,g62)
    c: Equal(g62,g65)
    c: Equal(g19,g63) = 1.7
    c: Coincident(g62,g68)
    c: Coincident(g64,g66)
    c: Equal(g66,g69)
    c: Equal(g25,g69) = 15
    c: Coincident(g53,g70)
    c: Coincident(g62,g70)
    c: Equal(g34,g70)
    c: Parallel(g70,g34)
    c: Coincident(g75,g76)
    c: Coincident(g76,g77)
    c: Coincident(g77,g78)
    c: Coincident(g78,g75)
    c: Horizontal(g75)
    c: Horizontal(g77)
    c: Vertical(g76)
    c: Vertical(g78)
    c: Coincident(g75,g72)
    c: Coincident(g76,g74)
    c: Equal(g73,g72)
    c: Equal(g72,g71)
    c: Equal(g71,g74)
    c: Equal(g19,g72) = 1.7
    c: Coincident(g71,g77)
    c: Coincident(g73,g75)
    c: Equal(g75,g78)
    c: Equal(g25,g78) = 15
    c: Coincident(g44,g79)
    c: Coincident(g71,g79)
    c: Equal(g52,g79)
    c: Perpendicular(g79,g34)
    c: Coincident(g84,g85)
    c: Coincident(g85,g86)
    c: Coincident(g86,g87)
    c: Coincident(g87,g84)
    c: Horizontal(g86)
    c: Vertical(g85)
    c: Vertical(g87)
    c: Coincident(g84,g81)
    c: Coincident(g85,g83)
    c: Equal(g82,g81)
    c: Equal(g81,g80)
    c: Equal(g80,g83)
    c: Equal(g19,g81) = 1.7
    c: Coincident(g80,g86)
    c: Coincident(g82,g84)
    c: Equal(g84,g87)
    c: Equal(g25,g87) = 15
    c: Coincident(g71,g88)
    c: Coincident(g80,g88)
    c: Equal(g34,g88)
    c: Parallel(g88,g34)
    c: Coincident(g93,g94)
    c: Coincident(g94,g95)
    c: Coincident(g95,g96)
    c: Coincident(g96,g93)
    c: Horizontal(g93)
    c: Horizontal(g95)
    c: Vertical(g94)
    c: Vertical(g96)
    c: Coincident(g93,g90)
    c: Coincident(g94,g92)
    c: Equal(g91,g90)
    c: Equal(g90,g89)
    c: Equal(g89,g92)
    c: Equal(g19,g90) = 1.7
    c: Coincident(g89,g95)
    c: Coincident(g91,g93)
    c: Equal(g93,g96)
    c: Equal(g25,g96) = 15
    c: Coincident(g80,g97)
    c: Coincident(g89,g97)
    c: Equal(g34,g97)
    c: Parallel(g97,g34)
    c: Symmetric(g82,g81,g-2)
    c: Coincident(g102,g103)
    c: Coincident(g103,g104)
    c: Coincident(g104,g105)
    c: Coincident(g105,g102)
    c: Horizontal(g104)
    c: Vertical(g105)
    c: Coincident(g102,g99)
    c: Coincident(g103,g101)
    c: Equal(g100,g99)
    c: Equal(g99,g98)
    c: Equal(g98,g101)
    c: Coincident(g98,g104)
    c: Coincident(g100,g102)
    c: Equal(g102,g105)
    c: Equal(g101,g81)
    c: Equal(g102,g93)
    c: Symmetric(g99,g100,g-2)
    c: Symmetric(g101,g100,g82)
    c: Coincident(g106,g0)
    c: Coincident(g106,g4)
    c: Coincident(g111,g107)
    c: Coincident(g111,g108)
    c: Horizontal(g111)
    c: Coincident(g112,g109)
    c: Coincident(g113,g109)
    c: Coincident(g113,g110)
    c: Horizontal(g113)
    c: Equal(g110,g109)
    c: Equal(g109,g108)
    c: Equal(g108,g107)
    c: Radius(g107) = 1.7
    c: Coincident(g108,g112)
    c: DistanceX(g107,g110) = 50
    c: Symmetric(g108,g109,g-2)
    c: DistanceX(g108,g109) = 15
    c: DistanceY(g0,g107) = 3
FEATURE [PartDesign::Pad] Pad004  label="TimonePortaBatterie001"
  AllowMultiFace = false
  Direction = (1,1,1)
  Length = 4
  Length2 = 100
  Profile = -> Sketch023
  Type = 0
FEATURE [Sketcher::SketchObject] Sketch024  label="TimonePortaBatterie003"
  FullyConstrained = false
  MapMode = 5
  Placement = pos=(0,0,4) rot=(0,0,1;0rad)
  Support = -> [Pad004]
  sketch-geometry (48):
    g0: LineSegment StartX=-52.5 StartY=0 StartZ=0 EndX=-30.5 EndY=0 EndZ=0
    g1: LineSegment StartX=-30.5 StartY=0 StartZ=0 EndX=-30.5 EndY=6.5 EndZ=0
    g2: LineSegment StartX=-30.5 StartY=6.5 StartZ=0 EndX=30.5 EndY=6.5 EndZ=0
    g3: LineSegment StartX=30.5 StartY=6.5 StartZ=0 EndX=30.5 EndY=0 EndZ=0
    g4: LineSegment StartX=30.5 StartY=0 StartZ=0 EndX=52.5 EndY=0 EndZ=0
    g5: LineSegment StartX=52.5 StartY=0 StartZ=0 EndX=52.5 EndY=76.5 EndZ=0
    g6: LineSegment StartX=42.5 StartY=98.8607 StartZ=0 EndX=30 EndY=110.041 EndZ=0
    g7: LineSegment StartX=-30 StartY=110.041 StartZ=0 EndX=-42.5 EndY=98.8607 EndZ=0
    g8: LineSegment StartX=-52.5 StartY=76.5 StartZ=0 EndX=-52.5 EndY=0 EndZ=0
    g9: ArcOfCircle CenterX=0 CenterY=76.5 CenterZ=0 NormalX=0 NormalY=0 NormalZ=1 AngleXU=0 Radius=45 StartAngle=0.841069 EndAngle=2.30052
    g10: LineSegment StartX=-30 StartY=110.041 StartZ=0 EndX=30 EndY=110.041 EndZ=0
    g11: ArcOfCircle CenterX=-22.5 CenterY=76.5 CenterZ=0 NormalX=0 NormalY=0 NormalZ=1 AngleXU=0 Radius=30 StartAngle=2.30052 EndAngle=3.14159
    g12: ArcOfCircle CenterX=22.5 CenterY=76.5 CenterZ=0 NormalX=0 NormalY=0 NormalZ=1 AngleXU=0 Radius=30 StartAngle=1e-16 EndAngle=0.841069
    g13: LineSegment StartX=-52.5 StartY=76.5 StartZ=0 EndX=52.5 EndY=76.5 EndZ=0
    g14: LineSegment StartX=-42.5 StartY=98.8607 StartZ=0 EndX=42.5 EndY=98.8607 EndZ=0
    g15: LineSegment StartX=-52.5 StartY=76.5 StartZ=0 EndX=-52.5 EndY=121.5 EndZ=0
    g16: LineSegment StartX=-52.5 StartY=121.5 StartZ=0 EndX=52.5 EndY=121.5 EndZ=0
    g17: LineSegment StartX=52.5 StartY=121.5 StartZ=0 EndX=52.5 EndY=76.5 EndZ=0
    g18: LineSegment StartX=-30.5 StartY=0 StartZ=0 EndX=30.5 EndY=0 EndZ=0
    g19: Circle CenterX=-24.8274 CenterY=3 CenterZ=0 NormalX=0 NormalY=0 NormalZ=1 AngleXU=0 Radius=1.7
    g20: Circle CenterX=-7.5 CenterY=3 CenterZ=0 NormalX=0 NormalY=0 NormalZ=1 AngleXU=0 Radius=1.7
    g21: Circle CenterX=7.5 CenterY=3 CenterZ=0 NormalX=0 NormalY=0 NormalZ=1 AngleXU=0 Radius=1.7
    g22: Circle CenterX=25.1726 CenterY=3 CenterZ=0 NormalX=0 NormalY=0 NormalZ=1 AngleXU=0 Radius=1.7
    g23: LineSegment StartX=-24.8274 StartY=3 StartZ=0 EndX=-7.5 EndY=3 EndZ=0
    g24: LineSegment StartX=-7.5 StartY=3 StartZ=0 EndX=7.5 EndY=3 EndZ=0
    g25: LineSegment StartX=7.5 StartY=3 StartZ=0 EndX=25.1726 EndY=3 EndZ=0
    g26: LineSegment StartX=-50.5 StartY=2 StartZ=0 EndX=-50.5 EndY=76.5 EndZ=0
    g27: LineSegment StartX=-40.1262 StartY=98.8607 StartZ=0 EndX=-26.9073 EndY=110.041 EndZ=0
    g28: LineSegment StartX=26.9073 StartY=110.041 StartZ=0 EndX=40.1262 EndY=98.8607 EndZ=0
    g29: LineSegment StartX=50.5 StartY=76.5 StartZ=0 EndX=50.5 EndY=2.77908 EndZ=0
    g30: LineSegment StartX=50.5 StartY=2.77908 StartZ=0 EndX=35.5 EndY=2.77908 EndZ=0
    g31: LineSegment StartX=32.5 StartY=5.77908 StartZ=0 EndX=32.5 EndY=9.5 EndZ=0
    g32: LineSegment StartX=32.5 StartY=9.5 StartZ=0 EndX=-32.5 EndY=9.5 EndZ=0
    g33: LineSegment StartX=-32.5 StartY=9.5 StartZ=0 EndX=-32.5 EndY=5 EndZ=0
    g34: LineSegment StartX=-35.5 StartY=2 StartZ=0 EndX=-50.5 EndY=2 EndZ=0
    g35: ArcOfCircle CenterX=-21.2139 CenterY=76.5 CenterZ=0 NormalX=0 NormalY=0 NormalZ=1 AngleXU=0 Radius=29.2861 StartAngle=2.27284 EndAngle=3.14159
    g36: ArcOfCircle CenterX=21.2139 CenterY=76.5 CenterZ=0 NormalX=0 NormalY=0 NormalZ=1 AngleXU=0 Radius=29.2861 StartAngle=0 EndAngle=0.868755
    g37: ArcOfCircle CenterX=0 CenterY=76.5 CenterZ=0 NormalX=0 NormalY=0 NormalZ=1 AngleXU=0 Radius=43 StartAngle=0.894703 EndAngle=2.24689
    g38: LineSegment StartX=-50.5 StartY=2 StartZ=0 EndX=-50.5 EndY=0 EndZ=0
    g39: LineSegment StartX=-30.5 StartY=6.5 StartZ=0 EndX=-32.5 EndY=6.5 EndZ=0
    g40: LineSegment StartX=32.5 StartY=2.77908 StartZ=0 EndX=30.5 EndY=2.77908 EndZ=0
    g41: LineSegment StartX=50.5 StartY=2.77908 StartZ=0 EndX=52.5 EndY=2.77908 EndZ=0
    g42: LineSegment StartX=0.211269 StartY=121.5 StartZ=0 EndX=0.211269 EndY=119.5 EndZ=0
    g43: LineSegment StartX=-30.5 StartY=6.5 StartZ=0 EndX=-30.5 EndY=9.5 EndZ=0
    g44: ArcOfCircle CenterX=-35.5 CenterY=5 CenterZ=0 NormalX=0 NormalY=0 NormalZ=1 AngleXU=0 Radius=3 StartAngle=4.71239 EndAngle=6.28319
    g45: ArcOfCircle CenterX=35.5 CenterY=5.77908 CenterZ=0 NormalX=0 NormalY=0 NormalZ=1 AngleXU=0 Radius=3 StartAngle=3.14159 EndAngle=4.71239
    g46: LineSegment StartX=32.5 StartY=5.77908 StartZ=0 EndX=32.5 EndY=2.77908 EndZ=0
    g47: LineSegment StartX=32.5 StartY=2.77908 StartZ=0 EndX=35.5 EndY=2.77908 EndZ=0
  constraints (124):
    c: Horizontal(g0)
    c: Coincident(g0,g1)
    c: Vertical(g1)
    c: Coincident(g1,g2)
    c: Coincident(g2,g3)
    c: Vertical(g3)
    c: Coincident(g3,g4)
    c: Horizontal(g4)
    c: Coincident(g4,g5)
    c: Vertical(g5)
    c: Coincident(g8,g0)
    c: Vertical(g8)
    c: PointOnObject(g9,g-2)
    c: Tangent(g9,g6) = -1.5708
    c: Coincident(g10,g7)
    c: Coincident(g10,g6)
    c: Horizontal(g10)
    c: Tangent(g7,g11) = -1.5708
    c: Tangent(g8,g11) = -1.5708
    c: Tangent(g6,g12) = -1.5708
    c: Tangent(g5,g12) = -1.5708
    c: Equal(g12,g11)
    c: Coincident(g13,g8)
    c: Coincident(g13,g5)
    c: Horizontal(g13)
    c: Coincident(g14,g7)
    c: Coincident(g14,g6)
    c: Tangent(g7,g9) = -1.5708
    c: PointOnObject(g0,g-1)
    c: PointOnObject(g4,g-1)
    c: DistanceY(g-1,g2) = 6.5
    c: DistanceX(g1,g2) = 61
    c: Symmetric(g1,g2,g-2)
    c: DistanceX(g0,g4) = 105
    c: DistanceY(g2,g5) = 70
    c: Radius(g9) = 45
    c: Radius(g11) = 30
    c: Coincident(g8,g15)
    c: Vertical(g15)
    c: Coincident(g15,g16)
    c: Horizontal(g16)
    c: Tangent(g16,g9)
    c: Coincident(g16,g17)
    c: Coincident(g17,g5)
    c: Vertical(g17)
    c: DistanceY(g5,g16) = 45
    c: Coincident(g18,g0)
    c: Coincident(g18,g4)
    c: Coincident(g23,g19)
    c: Coincident(g23,g20)
    c: Horizontal(g23)
    c: Coincident(g24,g21)
    c: Coincident(g25,g21)
    c: Coincident(g25,g22)
    c: Horizontal(g25)
    c: Equal(g22,g21)
    c: Equal(g21,g20)
    c: Equal(g20,g19)
    c: Radius(g19) = 1.7
    c: Coincident(g20,g24)
    c: DistanceX(g19,g22) = 50
    c: Symmetric(g20,g21,g-2)
    c: DistanceX(g20,g21) = 15
    c: DistanceY(g0,g19) = 3
    c: Vertical(g26)
    c: Vertical(g29)
    c: Coincident(g29,g30)
    c: Coincident(g31,g32)
    c: Coincident(g32,g33)
    c: Coincident(g34,g26)
    c: Tangent(g26,g35) = 1.5708
    c: Tangent(g27,g35) = 1.5708
    c: Tangent(g28,g36) = 1.5708
    c: Tangent(g29,g36) = 1.5708
    c: Coincident(g37,g9)
    c: Coincident(g37,g27)
    c: PointOnObject(g27,g10)
    c: Coincident(g37,g28)
    c: PointOnObject(g28,g10)
    c: PointOnObject(g26,g13)
    c: PointOnObject(g29,g13)
    c: Horizontal(g32)
    c: Vertical(g33)
    c: Horizontal(g34)
    c: Horizontal(g30)
    c: Vertical(g31)
    c: DistanceX(g0,g26) = 2
    c: DistanceY(g0,g26) = 2
    c: Coincident(g38,g26)
    c: PointOnObject(g38,g0)
    c: Vertical(g38)
    c: Coincident(g39,g1)
    c: PointOnObject(g39,g33)
    c: Horizontal(g39)
    c: Equal(g39,g38)
    c: PointOnObject(g40,g3)
    c: Horizontal(g40)
    c: Coincident(g41,g29)
    c: PointOnObject(g41,g5)
    c: Horizontal(g41)
    c: Equal(g41,g40)
    c: Equal(g40,g38)
    c: PointOnObject(g27,g14)
    c: PointOnObject(g28,g14)
    c: PointOnObject(g42,g9)
    c: PointOnObject(g42,g37)
    c: Vertical(g42)
    c: DistanceY(g42,g42) = 2
    c: Coincident(g43,g1)
    c: PointOnObject(g43,g32)
    c: Vertical(g43)
    c: DistanceY(g43,g43) = 3
    c: Tangent(g34,g44) = 1.5708
    c: Tangent(g33,g44) = 1.5708
    c: Radius(g44) = 3
    c: Tangent(g31,g45) = 1.5708
    c: Tangent(g30,g45) = 1.5708
    c: Coincident(g46,g31)
    c: Coincident(g46,g40)
    c: Coincident(g47,g40)
    c: Coincident(g47,g30)
    c: Radius(g45) = 3
    c: Horizontal(g47)
    c: Vertical(g46)
FEATURE [PartDesign::Pad] Pad005  label="Timone Porta Batterie001"
  AllowMultiFace = false
  BaseFeature = -> Pad004
  Direction = (1,1,1)
  Length = 2
  Length2 = 100
  Profile = -> Sketch024
  Type = 0
FEATURE [Sketcher::SketchObject] Sketch025  label="TimonePortaBatterie004"
  FullyConstrained = false
  MapMode = 5
  Placement = pos=(0,0,6) rot=(0,0,1;0rad)
  Support = -> [Pad005]
  sketch-geometry (60):
    g0: LineSegment StartX=-52.5 StartY=0 StartZ=0 EndX=-30.5 EndY=0 EndZ=0
    g1: LineSegment StartX=-30.5 StartY=0 StartZ=0 EndX=-30.5 EndY=6.5 EndZ=0
    g2: LineSegment StartX=-20 StartY=6.5 StartZ=0 EndX=20 EndY=6.5 EndZ=0
    g3: LineSegment StartX=30.5 StartY=6.5 StartZ=0 EndX=30.5 EndY=0 EndZ=0
    g4: LineSegment StartX=30.5 StartY=0 StartZ=0 EndX=52.5 EndY=0 EndZ=0
    g5: LineSegment StartX=52.5 StartY=0 StartZ=0 EndX=52.5 EndY=76.5 EndZ=0
    g6: LineSegment StartX=42.5 StartY=98.8607 StartZ=0 EndX=30 EndY=110.041 EndZ=0
    g7: LineSegment StartX=-30 StartY=110.041 StartZ=0 EndX=-42.5 EndY=98.8607 EndZ=0
    g8: LineSegment StartX=-52.5 StartY=76.5 StartZ=0 EndX=-52.5 EndY=0 EndZ=0
    g9: ArcOfCircle CenterX=0 CenterY=76.5 CenterZ=0 NormalX=0 NormalY=0 NormalZ=1 AngleXU=0 Radius=45 StartAngle=0.841069 EndAngle=2.30052
    g10: LineSegment StartX=-30 StartY=110.041 StartZ=0 EndX=30 EndY=110.041 EndZ=0
    g11: ArcOfCircle CenterX=-22.5 CenterY=76.5 CenterZ=0 NormalX=0 NormalY=0 NormalZ=1 AngleXU=0 Radius=30 StartAngle=2.30052 EndAngle=3.14159
    g12: ArcOfCircle CenterX=22.5 CenterY=76.5 CenterZ=0 NormalX=0 NormalY=0 NormalZ=1 AngleXU=0 Radius=30 StartAngle=1e-16 EndAngle=0.841069
    g13: LineSegment StartX=-52.5 StartY=76.5 StartZ=0 EndX=52.5 EndY=76.5 EndZ=0
    g14: LineSegment StartX=-42.5 StartY=98.8607 StartZ=0 EndX=42.5 EndY=98.8607 EndZ=0
    g15: LineSegment StartX=-52.5 StartY=76.5 StartZ=0 EndX=-52.5 EndY=121.5 EndZ=0
    g16: LineSegment StartX=-52.5 StartY=121.5 StartZ=0 EndX=52.5 EndY=121.5 EndZ=0
    g17: LineSegment StartX=52.5 StartY=121.5 StartZ=0 EndX=52.5 EndY=76.5 EndZ=0
    g18: LineSegment StartX=-30.5 StartY=0 StartZ=0 EndX=30.5 EndY=0 EndZ=0
    g19: Circle CenterX=-24.8274 CenterY=3 CenterZ=0 NormalX=0 NormalY=0 NormalZ=1 AngleXU=0 Radius=1.7
    g20: Circle CenterX=-7.5 CenterY=3 CenterZ=0 NormalX=0 NormalY=0 NormalZ=1 AngleXU=0 Radius=1.7
    g21: Circle CenterX=7.5 CenterY=3 CenterZ=0 NormalX=0 NormalY=0 NormalZ=1 AngleXU=0 Radius=1.7
    g22: Circle CenterX=25.1726 CenterY=3 CenterZ=0 NormalX=0 NormalY=0 NormalZ=1 AngleXU=0 Radius=1.7
    g23: LineSegment StartX=-24.8274 StartY=3 StartZ=0 EndX=-7.5 EndY=3 EndZ=0
    g24: LineSegment StartX=-7.5 StartY=3 StartZ=0 EndX=7.5 EndY=3 EndZ=0
    g25: LineSegment StartX=7.5 StartY=3 StartZ=0 EndX=25.1726 EndY=3 EndZ=0
    g26: LineSegment StartX=-50.5 StartY=2 StartZ=0 EndX=-50.5 EndY=76.5 EndZ=0
    g27: LineSegment StartX=-40.1262 StartY=98.8607 StartZ=0 EndX=-26.9073 EndY=110.041 EndZ=0
    g28: LineSegment StartX=26.9073 StartY=110.041 StartZ=0 EndX=40.1262 EndY=98.8607 EndZ=0
    g29: LineSegment StartX=50.5 StartY=76.5 StartZ=0 EndX=50.5 EndY=2.77908 EndZ=0
    g30: LineSegment StartX=50.5 StartY=2.77908 StartZ=0 EndX=35.5 EndY=2.77908 EndZ=0
    g31: LineSegment StartX=32.5 StartY=5.77908 StartZ=0 EndX=32.5 EndY=9.5 EndZ=0
    g32: LineSegment StartX=20 StartY=9.5 StartZ=0 EndX=-20 EndY=9.5 EndZ=0
    g33: LineSegment StartX=-32.5 StartY=9.5 StartZ=0 EndX=-32.5 EndY=5 EndZ=0
    g34: LineSegment StartX=-35.5 StartY=2 StartZ=0 EndX=-50.5 EndY=2 EndZ=0
    g35: ArcOfCircle CenterX=-21.2139 CenterY=76.5 CenterZ=0 NormalX=0 NormalY=0 NormalZ=1 AngleXU=0 Radius=29.2861 StartAngle=2.27284 EndAngle=3.14159
    g36: ArcOfCircle CenterX=21.2139 CenterY=76.5 CenterZ=0 NormalX=0 NormalY=0 NormalZ=1 AngleXU=0 Radius=29.2861 StartAngle=0 EndAngle=0.868755
    g37: ArcOfCircle CenterX=0 CenterY=76.5 CenterZ=0 NormalX=0 NormalY=0 NormalZ=1 AngleXU=0 Radius=43 StartAngle=0.894703 EndAngle=2.24689
    g38: LineSegment StartX=-50.5 StartY=2 StartZ=0 EndX=-50.5 EndY=0 EndZ=0
    g39: LineSegment StartX=-30.5 StartY=6.5 StartZ=0 EndX=-32.5 EndY=6.5 EndZ=0
    g40: LineSegment StartX=32.5 StartY=2.77908 StartZ=0 EndX=30.5 EndY=2.77908 EndZ=0
    g41: LineSegment StartX=50.5 StartY=2.77908 StartZ=0 EndX=52.5 EndY=2.77908 EndZ=0
    g42: LineSegment StartX=0.211269 StartY=121.5 StartZ=0 EndX=0.211269 EndY=119.5 EndZ=0
    g43: LineSegment StartX=-30.5 StartY=6.5 StartZ=0 EndX=-30.5 EndY=9.5 EndZ=0
    g44: ArcOfCircle CenterX=-35.5 CenterY=5 CenterZ=0 NormalX=0 NormalY=0 NormalZ=1 AngleXU=0 Radius=3 StartAngle=4.71239 EndAngle=6.28319
    g45: ArcOfCircle CenterX=35.5 CenterY=5.77908 CenterZ=0 NormalX=0 NormalY=0 NormalZ=1 AngleXU=0 Radius=3 StartAngle=3.14159 EndAngle=4.71239
    g46: LineSegment StartX=32.5 StartY=5.77908 StartZ=0 EndX=32.5 EndY=2.77908 EndZ=0
    g47: LineSegment StartX=32.5 StartY=2.77908 StartZ=0 EndX=35.5 EndY=2.77908 EndZ=0
    g48: LineSegment StartX=52.5 StartY=2.77908 StartZ=0 EndX=52.5 EndY=0 EndZ=0
    g49: LineSegment StartX=30.5 StartY=6.5 StartZ=0 EndX=32.5 EndY=9.5 EndZ=0
    g50: LineSegment StartX=-32.5 StartY=9.5 StartZ=0 EndX=-30.5 EndY=6.5 EndZ=0
    g51: LineSegment StartX=-20 StartY=9.5 StartZ=0 EndX=-20 EndY=6.5 EndZ=0
    g52: LineSegment StartX=20 StartY=9.5 StartZ=0 EndX=20 EndY=6.5 EndZ=0
    g53: LineSegment StartX=-30.5 StartY=9.5 StartZ=0 EndX=-32.5 EndY=9.5 EndZ=0
    g54: LineSegment StartX=-30.5 StartY=9.5 StartZ=0 EndX=-20 EndY=9.5 EndZ=0
    g55: LineSegment StartX=-30.5 StartY=6.5 StartZ=0 EndX=-20 EndY=6.5 EndZ=0
    g56: LineSegment StartX=20 StartY=9.5 StartZ=0 EndX=32.5 EndY=9.5 EndZ=0
    g57: LineSegment StartX=20 StartY=6.5 StartZ=0 EndX=30.5 EndY=6.5 EndZ=0
    g58: LineSegment StartX=-50.5 StartY=2 StartZ=0 EndX=-52.5 EndY=2 EndZ=0
    g59: LineSegment StartX=-52.5 StartY=2 StartZ=0 EndX=-52.5 EndY=0 EndZ=0
  constraints (148):
    c: Horizontal(g0)
    c: Coincident(g0,g1)
    c: Vertical(g1)
    c: Vertical(g3)
    c: Coincident(g3,g4)
    c: Horizontal(g4)
    c: Coincident(g4,g5)
    c: Vertical(g5)
    c: Coincident(g8,g0)
    c: Vertical(g8)
    c: PointOnObject(g9,g-2)
    c: Tangent(g9,g6) = -1.5708
    c: Coincident(g10,g7)
    c: Coincident(g10,g6)
    c: Horizontal(g10)
    c: Tangent(g7,g11) = -1.5708
    c: Tangent(g8,g11) = -1.5708
    c: Tangent(g6,g12) = -1.5708
    c: Tangent(g5,g12) = -1.5708
    c: Equal(g12,g11)
    c: Coincident(g13,g8)
    c: Coincident(g13,g5)
    c: Horizontal(g13)
    c: Coincident(g14,g7)
    c: Coincident(g14,g6)
    c: Tangent(g7,g9) = -1.5708
    c: PointOnObject(g0,g-1)
    c: PointOnObject(g4,g-1)
    c: DistanceY(g-1,g3) = 6.5
    c: DistanceX(g1,g3) = 61
    c: DistanceX(g0,g4) = 105
    c: DistanceY(g3,g5) = 70
    c: Radius(g9) = 45
    c: Radius(g11) = 30
    c: Coincident(g8,g15)
    c: Vertical(g15)
    c: Coincident(g15,g16)
    c: Horizontal(g16)
    c: Tangent(g16,g9)
    c: Coincident(g16,g17)
    c: Coincident(g17,g5)
    c: Vertical(g17)
    c: DistanceY(g5,g16) = 45
    c: Coincident(g18,g0)
    c: Coincident(g18,g4)
    c: Coincident(g23,g19)
    c: Coincident(g23,g20)
    c: Horizontal(g23)
    c: Coincident(g24,g21)
    c: Coincident(g25,g21)
    c: Coincident(g25,g22)
    c: Horizontal(g25)
    c: Equal(g22,g21)
    c: Equal(g21,g20)
    c: Equal(g20,g19)
    c: Radius(g19) = 1.7
    c: Coincident(g20,g24)
    c: DistanceX(g19,g22) = 50
    c: Symmetric(g20,g21,g-2)
    c: DistanceX(g20,g21) = 15
    c: DistanceY(g0,g19) = 3
    c: Vertical(g26)
    c: Vertical(g29)
    c: Coincident(g29,g30)
    c: Coincident(g53,g33)
    c: Coincident(g34,g26)
    c: Tangent(g26,g35) = 1.5708
    c: Tangent(g27,g35) = 1.5708
    c: Tangent(g28,g36) = 1.5708
    c: Tangent(g29,g36) = 1.5708
    c: Coincident(g37,g9)
    c: Coincident(g37,g27)
    c: PointOnObject(g27,g10)
    c: Coincident(g37,g28)
    c: PointOnObject(g28,g10)
    c: PointOnObject(g26,g13)
    c: PointOnObject(g29,g13)
    c: Horizontal(g32)
    c: Vertical(g33)
    c: Horizontal(g34)
    c: Horizontal(g30)
    c: Vertical(g31)
    c: DistanceX(g0,g26) = 2
    c: DistanceY(g0,g26) = 2
    c: Coincident(g38,g26)
    c: PointOnObject(g38,g0)
    c: Vertical(g38)
    c: Coincident(g39,g1)
    c: PointOnObject(g39,g33)
    c: Horizontal(g39)
    c: Equal(g39,g38)
    c: PointOnObject(g40,g3)
    c: Horizontal(g40)
    c: Coincident(g41,g29)
    c: PointOnObject(g41,g5)
    c: Horizontal(g41)
    c: Equal(g41,g40)
    c: Equal(g40,g38)
    c: PointOnObject(g27,g14)
    c: PointOnObject(g28,g14)
    c: PointOnObject(g42,g9)
    c: PointOnObject(g42,g37)
    c: Vertical(g42)
    c: DistanceY(g42,g42) = 2
    c: Coincident(g43,g1)
    c: Vertical(g43)
    c: Tangent(g34,g44) = 1.5708
    c: Tangent(g33,g44) = 1.5708
    c: Radius(g44) = 3
    c: Tangent(g31,g45) = 1.5708
    c: Tangent(g30,g45) = 1.5708
    c: Coincident(g46,g31)
    c: Coincident(g46,g40)
    c: Coincident(g47,g40)
    c: Coincident(g47,g30)
    c: Radius(g45) = 3
    c: Horizontal(g47)
    c: Vertical(g46)
    c: Coincident(g48,g41)
    c: Coincident(g48,g4)
    c: Coincident(g49,g3)
    c: Coincident(g49,g31)
    c: Coincident(g50,g53)
    c: Coincident(g50,g1)
    c: Vertical(g51)
    c: Vertical(g52)
    c: PointOnObject(g32,g51)
    c: Coincident(g53,g43)
    c: Tangent(g32,g53)
    c: Coincident(g2,g51)
    c: Coincident(g54,g53)
    c: Coincident(g54,g32)
    c: Coincident(g55,g1)
    c: Coincident(g55,g2)
    c: Horizontal(g55)
    c: Coincident(g2,g52)
    c: Coincident(g32,g52)
    c: Coincident(g56,g32)
    c: Coincident(g56,g31)
    c: Horizontal(g56)
    c: Coincident(g57,g2)
    c: Coincident(g57,g3)
    c: Horizontal(g57)
    c: Coincident(g58,g34)
    c: PointOnObject(g58,g8)
    c: Horizontal(g58)
    c: Coincident(g59,g58)
    c: Coincident(g59,g0)
FEATURE [PartDesign::Pad] Pad006  label="Timone Porta Batterie002"
  AllowMultiFace = false
  BaseFeature = -> Pad005
  Direction = (1,1,1)
  Length = 25
  Length2 = 100
  Profile = -> Sketch025
  Type = 0
FEATURE [Sketcher::SketchObject] Sketch026  label="TimonePortaBatterie005"
  FullyConstrained = false
  MapMode = 5
  Placement = pos=(0,0,31) rot=(0,0,1;0rad)
  Support = -> [Pad006]
  sketch-geometry (51):
    g0: LineSegment StartX=-52.5 StartY=0 StartZ=0 EndX=-30.5 EndY=0 EndZ=0
    g1: LineSegment StartX=-30.5 StartY=0 StartZ=0 EndX=-30.5 EndY=6.5 EndZ=0
    g2: LineSegment StartX=-30.5 StartY=6.5 StartZ=0 EndX=30.5 EndY=6.5 EndZ=0
    g3: LineSegment StartX=30.5 StartY=6.5 StartZ=0 EndX=30.5 EndY=0 EndZ=0
    g4: LineSegment StartX=30.5 StartY=0 StartZ=0 EndX=52.5 EndY=0 EndZ=0
    g5: LineSegment StartX=52.5 StartY=0 StartZ=0 EndX=52.5 EndY=76.5 EndZ=0
    g6: LineSegment StartX=42.5 StartY=98.8607 StartZ=0 EndX=30 EndY=110.041 EndZ=0
    g7: LineSegment StartX=-30 StartY=110.041 StartZ=0 EndX=-42.5 EndY=98.8607 EndZ=0
    g8: LineSegment StartX=-52.5 StartY=76.5 StartZ=0 EndX=-52.5 EndY=0 EndZ=0
    g9: ArcOfCircle CenterX=0 CenterY=76.5 CenterZ=0 NormalX=0 NormalY=0 NormalZ=1 AngleXU=0 Radius=45 StartAngle=0.841069 EndAngle=2.30052
    g10: LineSegment StartX=-30 StartY=110.041 StartZ=0 EndX=30 EndY=110.041 EndZ=0
    g11: ArcOfCircle CenterX=-22.5 CenterY=76.5 CenterZ=0 NormalX=0 NormalY=0 NormalZ=1 AngleXU=0 Radius=30 StartAngle=2.30052 EndAngle=3.14159
    g12: ArcOfCircle CenterX=22.5 CenterY=76.5 CenterZ=0 NormalX=0 NormalY=0 NormalZ=1 AngleXU=0 Radius=30 StartAngle=1e-16 EndAngle=0.841069
    g13: LineSegment StartX=-52.5 StartY=76.5 StartZ=0 EndX=52.5 EndY=76.5 EndZ=0
    g14: LineSegment StartX=-42.5 StartY=98.8607 StartZ=0 EndX=42.5 EndY=98.8607 EndZ=0
    g15: LineSegment StartX=-52.5 StartY=76.5 StartZ=0 EndX=-52.5 EndY=121.5 EndZ=0
    g16: LineSegment StartX=-52.5 StartY=121.5 StartZ=0 EndX=52.5 EndY=121.5 EndZ=0
    g17: LineSegment StartX=52.5 StartY=121.5 StartZ=0 EndX=52.5 EndY=76.5 EndZ=0
    g18: LineSegment StartX=-30.5 StartY=0 StartZ=0 EndX=30.5 EndY=0 EndZ=0
    g19: Circle CenterX=-24.8274 CenterY=3 CenterZ=0 NormalX=0 NormalY=0 NormalZ=1 AngleXU=0 Radius=1.7
    g20: Circle CenterX=-7.5 CenterY=3 CenterZ=0 NormalX=0 NormalY=0 NormalZ=1 AngleXU=0 Radius=1.7
    g21: Circle CenterX=7.5 CenterY=3 CenterZ=0 NormalX=0 NormalY=0 NormalZ=1 AngleXU=0 Radius=1.7
    g22: Circle CenterX=25.1726 CenterY=3 CenterZ=0 NormalX=0 NormalY=0 NormalZ=1 AngleXU=0 Radius=1.7
    g23: LineSegment StartX=-24.8274 StartY=3 StartZ=0 EndX=-7.5 EndY=3 EndZ=0
    g24: LineSegment StartX=-7.5 StartY=3 StartZ=0 EndX=7.5 EndY=3 EndZ=0
    g25: LineSegment StartX=7.5 StartY=3 StartZ=0 EndX=25.1726 EndY=3 EndZ=0
    g26: LineSegment StartX=-50.5 StartY=2 StartZ=0 EndX=-50.5 EndY=76.5 EndZ=0
    g27: LineSegment StartX=-40.1262 StartY=98.8607 StartZ=0 EndX=-26.9073 EndY=110.041 EndZ=0
    g28: LineSegment StartX=26.9073 StartY=110.041 StartZ=0 EndX=40.1262 EndY=98.8607 EndZ=0
    g29: LineSegment StartX=50.5 StartY=76.5 StartZ=0 EndX=50.5 EndY=2.77908 EndZ=0
    g30: LineSegment StartX=50.5 StartY=2.77908 StartZ=0 EndX=35.5 EndY=2.77908 EndZ=0
    g31: LineSegment StartX=32.5 StartY=5.77908 StartZ=0 EndX=32.5 EndY=9.5 EndZ=0
    g32: LineSegment StartX=32.5 StartY=9.5 StartZ=0 EndX=-32.5 EndY=9.5 EndZ=0
    g33: LineSegment StartX=-32.5 StartY=9.5 StartZ=0 EndX=-32.5 EndY=5 EndZ=0
    g34: LineSegment StartX=-35.5 StartY=2 StartZ=0 EndX=-50.5 EndY=2 EndZ=0
    g35: ArcOfCircle CenterX=-21.2139 CenterY=76.5 CenterZ=0 NormalX=0 NormalY=0 NormalZ=1 AngleXU=0 Radius=29.2861 StartAngle=2.27284 EndAngle=3.14159
    g36: ArcOfCircle CenterX=21.2139 CenterY=76.5 CenterZ=0 NormalX=0 NormalY=0 NormalZ=1 AngleXU=0 Radius=29.2861 StartAngle=0 EndAngle=0.868755
    g37: ArcOfCircle CenterX=0 CenterY=76.5 CenterZ=0 NormalX=0 NormalY=0 NormalZ=1 AngleXU=0 Radius=43 StartAngle=0.894703 EndAngle=2.24689
    g38: LineSegment StartX=-50.5 StartY=2 StartZ=0 EndX=-50.5 EndY=0 EndZ=0
    g39: LineSegment StartX=-30.5 StartY=6.5 StartZ=0 EndX=-32.5 EndY=6.5 EndZ=0
    g40: LineSegment StartX=32.5 StartY=2.77908 StartZ=0 EndX=30.5 EndY=2.77908 EndZ=0
    g41: LineSegment StartX=50.5 StartY=2.77908 StartZ=0 EndX=52.5 EndY=2.77908 EndZ=0
    g42: LineSegment StartX=0.211269 StartY=121.5 StartZ=0 EndX=0.211269 EndY=119.5 EndZ=0
    g43: LineSegment StartX=-30.5 StartY=6.5 StartZ=0 EndX=-30.5 EndY=9.5 EndZ=0
    g44: ArcOfCircle CenterX=-35.5 CenterY=5 CenterZ=0 NormalX=0 NormalY=0 NormalZ=1 AngleXU=0 Radius=3 StartAngle=4.71239 EndAngle=6.28319
    g45: ArcOfCircle CenterX=35.5 CenterY=5.77908 CenterZ=0 NormalX=0 NormalY=0 NormalZ=1 AngleXU=0 Radius=3 StartAngle=3.14159 EndAngle=4.71239
    g46: LineSegment StartX=32.5 StartY=5.77908 StartZ=0 EndX=32.5 EndY=2.77908 EndZ=0
    g47: LineSegment StartX=32.5 StartY=2.77908 StartZ=0 EndX=35.5 EndY=2.77908 EndZ=0
    g48: LineSegment StartX=-52.5 StartY=0 StartZ=0 EndX=-52.5 EndY=2 EndZ=0
    g49: LineSegment StartX=-52.5 StartY=2 StartZ=0 EndX=-50.5 EndY=2 EndZ=0
    g50: LineSegment StartX=52.5 StartY=2.77908 StartZ=0 EndX=52.5 EndY=0 EndZ=0
  constraints (131):
    c: Horizontal(g0)
    c: Coincident(g0,g1)
    c: Vertical(g1)
    c: Coincident(g1,g2)
    c: Coincident(g2,g3)
    c: Vertical(g3)
    c: Coincident(g3,g4)
    c: Horizontal(g4)
    c: Coincident(g4,g5)
    c: Vertical(g5)
    c: Coincident(g8,g0)
    c: Vertical(g8)
    c: PointOnObject(g9,g-2)
    c: Tangent(g9,g6) = -1.5708
    c: Coincident(g10,g7)
    c: Coincident(g10,g6)
    c: Horizontal(g10)
    c: Tangent(g7,g11) = -1.5708
    c: Tangent(g8,g11) = -1.5708
    c: Tangent(g6,g12) = -1.5708
    c: Tangent(g5,g12) = -1.5708
    c: Equal(g12,g11)
    c: Coincident(g13,g8)
    c: Coincident(g13,g5)
    c: Horizontal(g13)
    c: Coincident(g14,g7)
    c: Coincident(g14,g6)
    c: Tangent(g7,g9) = -1.5708
    c: PointOnObject(g0,g-1)
    c: PointOnObject(g4,g-1)
    c: DistanceY(g-1,g2) = 6.5
    c: DistanceX(g1,g2) = 61
    c: Symmetric(g1,g2,g-2)
    c: DistanceX(g0,g4) = 105
    c: DistanceY(g2,g5) = 70
    c: Radius(g9) = 45
    c: Radius(g11) = 30
    c: Coincident(g8,g15)
    c: Vertical(g15)
    c: Coincident(g15,g16)
    c: Horizontal(g16)
    c: Tangent(g16,g9)
    c: Coincident(g16,g17)
    c: Coincident(g17,g5)
    c: Vertical(g17)
    c: DistanceY(g5,g16) = 45
    c: Coincident(g18,g0)
    c: Coincident(g18,g4)
    c: Coincident(g23,g19)
    c: Coincident(g23,g20)
    c: Horizontal(g23)
    c: Coincident(g24,g21)
    c: Coincident(g25,g21)
    c: Coincident(g25,g22)
    c: Horizontal(g25)
    c: Equal(g22,g21)
    c: Equal(g21,g20)
    c: Equal(g20,g19)
    c: Radius(g19) = 1.7
    c: Coincident(g20,g24)
    c: DistanceX(g19,g22) = 50
    c: Symmetric(g20,g21,g-2)
    c: DistanceX(g20,g21) = 15
    c: DistanceY(g0,g19) = 3
    c: Vertical(g26)
    c: Vertical(g29)
    c: Coincident(g29,g30)
    c: Coincident(g31,g32)
    c: Coincident(g32,g33)
    c: Coincident(g34,g26)
    c: Tangent(g26,g35) = 1.5708
    c: Tangent(g27,g35) = 1.5708
    c: Tangent(g28,g36) = 1.5708
    c: Tangent(g29,g36) = 1.5708
    c: Coincident(g37,g9)
    c: Coincident(g37,g27)
    c: PointOnObject(g27,g10)
    c: Coincident(g37,g28)
    c: PointOnObject(g28,g10)
    c: PointOnObject(g26,g13)
    c: PointOnObject(g29,g13)
    c: Horizontal(g32)
    c: Vertical(g33)
    c: Horizontal(g34)
    c: Horizontal(g30)
    c: Vertical(g31)
    c: DistanceX(g0,g26) = 2
    c: DistanceY(g0,g26) = 2
    c: Coincident(g38,g26)
    c: PointOnObject(g38,g0)
    c: Vertical(g38)
    c: Coincident(g39,g1)
    c: PointOnObject(g39,g33)
    c: Horizontal(g39)
    c: Equal(g39,g38)
    c: PointOnObject(g40,g3)
    c: Horizontal(g40)
    c: Coincident(g41,g29)
    c: PointOnObject(g41,g5)
    c: Horizontal(g41)
    c: Equal(g41,g40)
    c: Equal(g40,g38)
    c: PointOnObject(g27,g14)
    c: PointOnObject(g28,g14)
    c: PointOnObject(g42,g9)
    c: PointOnObject(g42,g37)
    c: Vertical(g42)
    c: DistanceY(g42,g42) = 2
    c: Coincident(g43,g1)
    c: PointOnObject(g43,g32)
    c: Vertical(g43)
    c: DistanceY(g43,g43) = 3
    c: Tangent(g34,g44) = 1.5708
    c: Tangent(g33,g44) = 1.5708
    c: Radius(g44) = 3
    c: Tangent(g31,g45) = 1.5708
    c: Tangent(g30,g45) = 1.5708
    c: Coincident(g46,g31)
    c: Coincident(g46,g40)
    c: Coincident(g47,g40)
    c: Coincident(g47,g30)
    c: Radius(g45) = 3
    c: Horizontal(g47)
    c: Vertical(g46)
    c: Coincident(g48,g0)
    c: Vertical(g48)
    c: Coincident(g49,g48)
    c: Coincident(g49,g34)
    c: Horizontal(g49)
    c: Coincident(g50,g41)
    c: Coincident(g50,g4)
FEATURE [PartDesign::Pad] Pad007  label="Timone Porta Batterie003"
  AllowMultiFace = false
  BaseFeature = -> Pad006
  Direction = (1,1,1)
  Length = 5
  Length2 = 100
  Profile = -> Sketch026
  Type = 0
FEATURE [Sketcher::SketchObject] Sketch027
  FullyConstrained = false
  MapMode = 5
  Placement = pos=(0,9.5,0) rot=(0,0.707107,0.707107;3.14159rad)
  Support = -> [Pad007]
  sketch-geometry (12):
    g0: Circle CenterX=-14.882 CenterY=23 CenterZ=0 NormalX=0 NormalY=0 NormalZ=1 AngleXU=0 Radius=1.7
    g1: Circle CenterX=0 CenterY=23 CenterZ=0 NormalX=0 NormalY=0 NormalZ=1 AngleXU=0 Radius=1.7
    g2: Circle CenterX=15.118 CenterY=23 CenterZ=0 NormalX=0 NormalY=0 NormalZ=1 AngleXU=0 Radius=1.7
    g3: Circle CenterX=15.118 CenterY=7 CenterZ=0 NormalX=0 NormalY=0 NormalZ=1 AngleXU=0 Radius=1.7
    g4: Circle CenterX=0 CenterY=7 CenterZ=0 NormalX=0 NormalY=0 NormalZ=1 AngleXU=0 Radius=1.7
    g5: Circle CenterX=-14.882 CenterY=7 CenterZ=0 NormalX=0 NormalY=0 NormalZ=1 AngleXU=0 Radius=1.7
    g6: LineSegment StartX=-14.882 StartY=23 StartZ=0 EndX=0 EndY=23 EndZ=0
    g7: LineSegment StartX=0 StartY=23 StartZ=0 EndX=15.118 EndY=23 EndZ=0
    g8: LineSegment StartX=15.118 StartY=23 StartZ=0 EndX=15.118 EndY=7 EndZ=0
    g9: LineSegment StartX=15.118 StartY=7 StartZ=0 EndX=0 EndY=7 EndZ=0
    g10: LineSegment StartX=0 StartY=7 StartZ=0 EndX=-14.882 EndY=7 EndZ=0
    g11: LineSegment StartX=-14.882 StartY=7 StartZ=0 EndX=-14.882 EndY=23 EndZ=0
  constraints (29):
    c: PointOnObject(g1,g-2)
    c: PointOnObject(g4,g-2)
    c: Coincident(g6,g0)
    c: Coincident(g6,g1)
    c: Horizontal(g6)
    c: Coincident(g6,g7)
    c: Coincident(g7,g2)
    c: Horizontal(g7)
    c: Coincident(g7,g8)
    c: Coincident(g8,g3)
    c: Vertical(g8)
    c: Coincident(g8,g9)
    c: Coincident(g9,g4)
    c: Coincident(g9,g10)
    c: Coincident(g10,g5)
    c: Horizontal(g10)
    c: Coincident(g10,g11)
    c: Coincident(g11,g6)
    c: Vertical(g11)
    c: Horizontal(g9)
    c: DistanceX(g0,g2) = 30
    c: DistanceY(g5,g0) = 16
    c: Equal(g0,g1)
    c: Equal(g1,g2)
    c: Equal(g2,g3)
    c: Equal(g3,g4)
    c: Equal(g4,g5)
    c: Radius(g0) = 1.7
    c: DistanceY(g-1,g5) = 7
FEATURE [PartDesign::Pocket] Pocket018  label="Timone Porta Batterie004"
  AllowMultiFace = false
  BaseFeature = -> Pad007
  Length = 10
  Length2 = 100
  Profile = -> Sketch027
  Type = 0
FEATURE [Sketcher::SketchObject] Sketch028  label="AsseAcciaio"
  FullyConstrained = false
  MapMode = 5
  Placement = pos=(42.6,0,0) rot=(0.707107,0,0.707107;3.14159rad)
  Support = -> [Pocket015]
  sketch-geometry (1):
    g0: Circle CenterX=0 CenterY=0 CenterZ=0 NormalX=0 NormalY=0 NormalZ=1 AngleXU=0 Radius=1
  constraints (2):
    c: Coincident(g0,g-1)
    c: Radius(g0) = 1
FEATURE [PartDesign::Pocket] Pocket019  label="RuoteDa90asse017"
  AllowMultiFace = false
  BaseFeature = -> Pocket015
  Length = 100
  Length2 = 100
  Placement = pos=(0,0,0) rot=(1,0,0;1.5708rad)
  Profile = -> Sketch028
  Type = 0
FEATURE [PartDesign::Body] Body001  label="RuoteDa90asse8"
  Group = -> [Sketch011,Revolution,Sketch013,Sketch017,Pocket014,Fillet001,Pocket015,Sketch028,Pocket019]
  Origin = -> Origin003
  Tip = -> Pocket019
FEATURE [App::Part] Part001  label="Ruote da 90 asse 8SX"
  Group = -> [Body001]
  Origin = -> Origin002
  Placement = pos=(-27,0,0) rot=(0,0,1;3.14159rad)
FEATURE [Sketcher::SketchObject] Sketch029  label="SupportoSfera001"
  FullyConstrained = false
  MapMode = 5
  Support = -> [XY_Plane011]
  sketch-geometry (9):
    g0: Circle CenterX=0 CenterY=-1e-16 CenterZ=0 NormalX=0 NormalY=0 NormalZ=1 AngleXU=0 Radius=16
    g1: Circle CenterX=0 CenterY=-1e-16 CenterZ=0 NormalX=0 NormalY=0 NormalZ=1 AngleXU=0 Radius=10
    g2: LineSegment StartX=10.3923 StartY=-6 StartZ=0 EndX=0 EndY=12 EndZ=0
    g3: LineSegment StartX=0 StartY=12 StartZ=0 EndX=-10.3923 EndY=-6 EndZ=0
    g4: LineSegment StartX=-10.3923 StartY=-6 StartZ=0 EndX=10.3923 EndY=-6 EndZ=0
    g5: Circle CenterX=0 CenterY=-1e-16 CenterZ=0 NormalX=0 NormalY=0 NormalZ=1 AngleXU=0 Radius=12
    g6: Circle CenterX=0 CenterY=12 CenterZ=0 NormalX=0 NormalY=0 NormalZ=1 AngleXU=0 Radius=1.7
    g7: Circle CenterX=-10.3923 CenterY=-6 CenterZ=0 NormalX=0 NormalY=0 NormalZ=1 AngleXU=0 Radius=1.7
    g8: Circle CenterX=10.3923 CenterY=-6 CenterZ=0 NormalX=0 NormalY=0 NormalZ=1 AngleXU=0 Radius=1.7
  constraints (21):
    c: Coincident(g0,g-1)
    c: Coincident(g1,g0)
    c: Coincident(g2,g3)
    c: Coincident(g3,g4)
    c: Coincident(g4,g2)
    c: Equal(g2,g3)
    c: Equal(g2,g4)
    c: PointOnObject(g2,g5)
    c: PointOnObject(g3,g5)
    c: PointOnObject(g4,g5)
    c: Coincident(g5,g0)
    c: PointOnObject(g2,g-2)
    c: Radius(g0) = 16
    c: Radius(g5) = 12
    c: Coincident(g6,g2)
    c: Coincident(g7,g3)
    c: Coincident(g8,g2)
    c: Equal(g7,g8)
    c: Radius(g6) = 1.7
    c: Equal(g6,g7)
    c: Radius(g1) = 10
FEATURE [PartDesign::Pad] Pad008
  AllowMultiFace = false
  Direction = (1,1,1)
  Length = 7
  Length2 = 100
  Profile = -> Sketch029
  Type = 0
FEATURE [Sketcher::SketchObject] Sketch030  label="SupportoSfera002"
  FullyConstrained = false
  MapMode = 5
  Placement = pos=(0,0,7) rot=(0,0,1;0rad)
  Support = -> [Pad008]
  sketch-geometry (21):
    g0: Circle CenterX=0 CenterY=-1e-16 CenterZ=0 NormalX=0 NormalY=0 NormalZ=1 AngleXU=0 Radius=16
    g1: Circle CenterX=0 CenterY=-1e-16 CenterZ=0 NormalX=0 NormalY=0 NormalZ=1 AngleXU=0 Radius=10
    g2: LineSegment StartX=10.3923 StartY=-6 StartZ=0 EndX=0 EndY=12 EndZ=0
    g3: LineSegment StartX=0 StartY=12 StartZ=0 EndX=-10.3923 EndY=-6 EndZ=0
    g4: LineSegment StartX=-10.3923 StartY=-6 StartZ=0 EndX=10.3923 EndY=-6 EndZ=0
    g5: Circle CenterX=0 CenterY=-1e-16 CenterZ=0 NormalX=0 NormalY=0 NormalZ=1 AngleXU=0 Radius=12
    g6: Circle CenterX=0 CenterY=12 CenterZ=0 NormalX=0 NormalY=0 NormalZ=1 AngleXU=0 Radius=1.7
    g7: Circle CenterX=-10.3923 CenterY=-6 CenterZ=0 NormalX=0 NormalY=0 NormalZ=1 AngleXU=0 Radius=1.7
    g8: Circle CenterX=10.3923 CenterY=-6 CenterZ=0 NormalX=0 NormalY=0 NormalZ=1 AngleXU=0 Radius=1.7
    g9: ArcOfCircle CenterX=-12.5 CenterY=0 CenterZ=0 NormalX=0 NormalY=0 NormalZ=1 AngleXU=0 Radius=16 StartAngle=1.5708 EndAngle=4.71239
    g10: ArcOfCircle CenterX=12.5 CenterY=3e-16 CenterZ=0 NormalX=0 NormalY=0 NormalZ=1 AngleXU=0 Radius=16 StartAngle=4.71239 EndAngle=7.85398
    g11: LineSegment StartX=-12.5 StartY=-16 StartZ=0 EndX=12.5 EndY=-16 EndZ=0
    g12: LineSegment StartX=-12.5 StartY=16 StartZ=0 EndX=12.5 EndY=16 EndZ=0
    g13: Circle CenterX=-17.4858 CenterY=7.64555 CenterZ=0 NormalX=0 NormalY=0 NormalZ=1 AngleXU=0 Radius=1.8
    g14: Circle CenterX=-17.4858 CenterY=-7.64555 CenterZ=0 NormalX=0 NormalY=0 NormalZ=1 AngleXU=0 Radius=1.8
    g15: Circle CenterX=17.4858 CenterY=-7.64555 CenterZ=0 NormalX=0 NormalY=0 NormalZ=1 AngleXU=0 Radius=1.8
    g16: Circle CenterX=17.4858 CenterY=7.64555 CenterZ=0 NormalX=0 NormalY=0 NormalZ=1 AngleXU=0 Radius=1.8
    g17: LineSegment StartX=-17.4858 StartY=7.64555 StartZ=0 EndX=17.4858 EndY=7.64555 EndZ=0
    g18: LineSegment StartX=17.4858 StartY=7.64555 StartZ=0 EndX=17.4858 EndY=-7.64555 EndZ=0
    g19: LineSegment StartX=17.4858 StartY=-7.64555 StartZ=0 EndX=-17.4858 EndY=-7.64555 EndZ=0
    g20: LineSegment StartX=-17.4858 StartY=-7.64555 StartZ=0 EndX=-17.4858 EndY=7.64555 EndZ=0
  constraints (46):
    c: Coincident(g0,g-1)
    c: Coincident(g1,g0)
    c: Coincident(g2,g3)
    c: Coincident(g3,g4)
    c: Coincident(g4,g2)
    c: Equal(g2,g3)
    c: Equal(g2,g4)
    c: PointOnObject(g2,g5)
    c: PointOnObject(g3,g5)
    c: PointOnObject(g4,g5)
    c: Coincident(g5,g0)
    c: PointOnObject(g2,g-2)
    c: Radius(g0) = 16
    c: Radius(g5) = 12
    c: Coincident(g6,g2)
    c: Coincident(g7,g3)
    c: Coincident(g8,g2)
    c: Equal(g7,g8)
    c: Radius(g6) = 1.7
    c: Equal(g6,g7)
    c: Radius(g1) = 10
    c: Tangent(g9,g12) = 1.5708
    c: Tangent(g9,g11) = -1.5708
    c: Tangent(g11,g10) = -1.5708
    c: Tangent(g12,g10) = 1.5708
    c: Horizontal(g11)
    c: PointOnObject(g9,g-1)
    c: Symmetric(g10,g9,g-2)
    c: DistanceY(g10,g10) = 32
    c: DistanceX(g9,g10) = 25
    c: Coincident(g17,g18)
    c: Coincident(g18,g19)
    c: Coincident(g19,g20)
    c: Coincident(g20,g17)
    c: Horizontal(g19)
    c: Vertical(g18)
    c: Coincident(g17,g13)
    c: Coincident(g18,g15)
    c: Coincident(g19,g14)
    c: Coincident(g17,g16)
    c: Equal(g16,g13)
    c: Equal(g13,g14)
    c: Symmetric(g13,g16,g-2)
    c: Symmetric(g13,g14,g-1)
    c: Equal(g15,g16)
    c: Radius(g13) = 1.8
FEATURE [PartDesign::Pad] Pad009
  AllowMultiFace = false
  BaseFeature = -> Pad008
  Direction = (1,1,1)
  Length = 15
  Length2 = 100
  Profile = -> Sketch030
  Type = 0
FEATURE [Sketcher::SketchObject] Sketch031  label="SupportoSfera003"
  FullyConstrained = false
  MapMode = 5
  Placement = pos=(0,0,22) rot=(0,0,1;0rad)
  Support = -> [Pad009]
  sketch-geometry (21):
    g0: Circle CenterX=0 CenterY=-1e-16 CenterZ=0 NormalX=0 NormalY=0 NormalZ=1 AngleXU=0 Radius=16
    g1: Circle CenterX=0 CenterY=-1e-16 CenterZ=0 NormalX=0 NormalY=0 NormalZ=1 AngleXU=0 Radius=10
    g2: LineSegment StartX=10.3923 StartY=-6 StartZ=0 EndX=0 EndY=12 EndZ=0
    g3: LineSegment StartX=0 StartY=12 StartZ=0 EndX=-10.3923 EndY=-6 EndZ=0
    g4: LineSegment StartX=-10.3923 StartY=-6 StartZ=0 EndX=10.3923 EndY=-6 EndZ=0
    g5: Circle CenterX=0 CenterY=-1e-16 CenterZ=0 NormalX=0 NormalY=0 NormalZ=1 AngleXU=0 Radius=12
    g6: Circle CenterX=0 CenterY=12 CenterZ=0 NormalX=0 NormalY=0 NormalZ=1 AngleXU=0 Radius=1.7
    g7: Circle CenterX=-10.3923 CenterY=-6 CenterZ=0 NormalX=0 NormalY=0 NormalZ=1 AngleXU=0 Radius=1.7
    g8: Circle CenterX=10.3923 CenterY=-6 CenterZ=0 NormalX=0 NormalY=0 NormalZ=1 AngleXU=0 Radius=1.7
    g9: ArcOfCircle CenterX=-12.5 CenterY=0 CenterZ=0 NormalX=0 NormalY=0 NormalZ=1 AngleXU=0 Radius=16 StartAngle=1.5708 EndAngle=4.71239
    g10: ArcOfCircle CenterX=12.5 CenterY=3e-16 CenterZ=0 NormalX=0 NormalY=0 NormalZ=1 AngleXU=0 Radius=16 StartAngle=4.71239 EndAngle=7.85398
    g11: LineSegment StartX=-12.5 StartY=-16 StartZ=0 EndX=12.5 EndY=-16 EndZ=0
    g12: LineSegment StartX=-12.5 StartY=16 StartZ=0 EndX=12.5 EndY=16 EndZ=0
    g13: Circle CenterX=-17.4918 CenterY=7.55431 CenterZ=0 NormalX=0 NormalY=0 NormalZ=1 AngleXU=0 Radius=1.8
    g14: Circle CenterX=-17.4918 CenterY=-7.55431 CenterZ=0 NormalX=0 NormalY=0 NormalZ=1 AngleXU=0 Radius=1.8
    g15: Circle CenterX=17.4918 CenterY=-7.55431 CenterZ=0 NormalX=0 NormalY=0 NormalZ=1 AngleXU=0 Radius=1.8
    g16: Circle CenterX=17.4918 CenterY=7.55431 CenterZ=0 NormalX=0 NormalY=0 NormalZ=1 AngleXU=0 Radius=1.8
    g17: LineSegment StartX=-17.4918 StartY=7.55431 StartZ=0 EndX=17.4918 EndY=7.55431 EndZ=0
    g18: LineSegment StartX=17.4918 StartY=7.55431 StartZ=0 EndX=17.4918 EndY=-7.55431 EndZ=0
    g19: LineSegment StartX=17.4918 StartY=-7.55431 StartZ=0 EndX=-17.4918 EndY=-7.55431 EndZ=0
    g20: LineSegment StartX=-17.4918 StartY=-7.55431 StartZ=0 EndX=-17.4918 EndY=7.55431 EndZ=0
  constraints (46):
    c: Coincident(g0,g-1)
    c: Coincident(g1,g0)
    c: Coincident(g2,g3)
    c: Coincident(g3,g4)
    c: Coincident(g4,g2)
    c: Equal(g2,g3)
    c: Equal(g2,g4)
    c: PointOnObject(g2,g5)
    c: PointOnObject(g3,g5)
    c: PointOnObject(g4,g5)
    c: Coincident(g5,g0)
    c: PointOnObject(g2,g-2)
    c: Radius(g0) = 16
    c: Radius(g5) = 12
    c: Coincident(g6,g2)
    c: Coincident(g7,g3)
    c: Coincident(g8,g2)
    c: Equal(g7,g8)
    c: Radius(g6) = 1.7
    c: Equal(g6,g7)
    c: Radius(g1) = 10
    c: Tangent(g9,g12) = 1.5708
    c: Tangent(g9,g11) = -1.5708
    c: Tangent(g11,g10) = -1.5708
    c: Tangent(g12,g10) = 1.5708
    c: Horizontal(g11)
    c: PointOnObject(g9,g-1)
    c: Symmetric(g10,g9,g-2)
    c: DistanceY(g10,g10) = 32
    c: DistanceX(g9,g10) = 25
    c: Coincident(g17,g18)
    c: Coincident(g18,g19)
    c: Coincident(g19,g20)
    c: Coincident(g20,g17)
    c: Horizontal(g19)
    c: Vertical(g18)
    c: Coincident(g17,g13)
    c: Coincident(g18,g15)
    c: Coincident(g19,g14)
    c: Coincident(g17,g16)
    c: Equal(g16,g13)
    c: Equal(g13,g14)
    c: Symmetric(g13,g16,g-2)
    c: Symmetric(g13,g14,g-1)
    c: Equal(g15,g16)
    c: Radius(g13) = 1.8
FEATURE [PartDesign::Pocket] Pocket020
  AllowMultiFace = false
  BaseFeature = -> Pad009
  Length = 30
  Length2 = 100
  Profile = -> Sketch031
  Type = 0
FEATURE [Sketcher::SketchObject] Sketch032
  FullyConstrained = false
  MapMode = 5
  Placement = pos=(0,16,0) rot=(0,0.707107,0.707107;3.14159rad)
  Support = -> [Pocket020]
  sketch-geometry (15):
    g0: LineSegment StartX=-23 StartY=21.7525 StartZ=0 EndX=23 EndY=21.7525 EndZ=0
    g1: LineSegment StartX=23 StartY=21.7525 StartZ=0 EndX=23 EndY=0.077331 EndZ=0
    g2: LineSegment StartX=23 StartY=0.077331 StartZ=0 EndX=-23 EndY=0.077331 EndZ=0
    g3: LineSegment StartX=-23 StartY=0.077331 StartZ=0 EndX=-23 EndY=21.7525 EndZ=0
    g4: LineSegment StartX=-72.7015 StartY=-8.2472 StartZ=0 EndX=89.5485 EndY=-8.2472 EndZ=0
    g5: ArcOfCircle CenterX=-17 CenterY=16 CenterZ=0 NormalX=0 NormalY=0 NormalZ=1 AngleXU=0 Radius=0.4 StartAngle=-5.3e-15 EndAngle=3.14159
    g6: ArcOfCircle CenterX=-17 CenterY=4 CenterZ=0 NormalX=0 NormalY=0 NormalZ=1 AngleXU=0 Radius=0.4 StartAngle=3.14159 EndAngle=6.28319
    g7: LineSegment StartX=-17.4 StartY=16 StartZ=0 EndX=-17.4 EndY=4 EndZ=0
    g8: LineSegment StartX=-16.6 StartY=16 StartZ=0 EndX=-16.6 EndY=4 EndZ=0
    g9: ArcOfCircle CenterX=17 CenterY=16 CenterZ=0 NormalX=0 NormalY=0 NormalZ=1 AngleXU=0 Radius=0.4 StartAngle=0 EndAngle=3.14159
    g10: ArcOfCircle CenterX=17 CenterY=4 CenterZ=0 NormalX=0 NormalY=0 NormalZ=1 AngleXU=0 Radius=0.4 StartAngle=3.14159 EndAngle=6.28319
    g11: LineSegment StartX=16.6 StartY=16 StartZ=0 EndX=16.6 EndY=4 EndZ=0
    g12: LineSegment StartX=17.4 StartY=16 StartZ=0 EndX=17.4 EndY=4 EndZ=0
    g13: LineSegment StartX=-16.6 StartY=16 StartZ=0 EndX=16.6 EndY=16 EndZ=0
    g14: LineSegment StartX=-16.6 StartY=4 StartZ=0 EndX=16.6 EndY=4 EndZ=0
  constraints (33):
    c: Coincident(g0,g1)
    c: Coincident(g1,g2)
    c: Coincident(g2,g3)
    c: Coincident(g3,g0)
    c: Horizontal(g0)
    c: Vertical(g1)
    c: Vertical(g3)
    c: Horizontal(g4)
    c: Symmetric(g2,g1,g-2)
    c: DistanceX(g2,g1) = 46
    c: Tangent(g5,g8) = 1.5708
    c: Tangent(g5,g7) = -1.5708
    c: Tangent(g7,g6) = -1.5708
    c: Tangent(g8,g6) = 1.5708
    c: Vertical(g7)
    c: Equal(g5,g6)
    c: Tangent(g9,g12) = 1.5708
    c: Tangent(g9,g11) = -1.5708
    c: Tangent(g11,g10) = -1.5708
    c: Tangent(g12,g10) = 1.5708
    c: Vertical(g11)
    c: Equal(g9,g10)
    c: Equal(g9,g5)
    c: Coincident(g13,g5)
    c: Coincident(g13,g9)
    c: Horizontal(g13)
    c: Coincident(g14,g6)
    c: Coincident(g14,g10)
    c: Symmetric(g10,g6,g-2)
    c: DistanceX(g6,g10) = 34
    c: Radius(g6) = 0.4
    c: DistanceY(g6,g5) = 12
    c: DistanceY(g-1,g6) = 4
FEATURE [PartDesign::Pad] Pad010
  AllowMultiFace = false
  BaseFeature = -> Pocket020
  Direction = (1,1,1)
  Length = 5
  Length2 = 100
  Profile = -> Sketch032
  Type = 0
FEATURE [PartDesign::Body] Body005  label="SupportoSfera"
  Group = -> [Sketch029,Pad008,Sketch030,Pad009,Sketch031,Pocket020,Sketch032,Pad010]
  Origin = -> Origin011
  Tip = -> Pad010
FEATURE [App::Part] Part005  label="Supporto Sfera"
  Group = -> [Body005]
  Origin = -> Origin010
  Placement = pos=(0,115.5,-37) rot=(0,0,1;0rad)
FEATURE [Sketcher::SketchObject] Sketch033  label="TimonePortaBatterie006"
  FullyConstrained = true
  MapMode = 5
  Placement = pos=(0,0,4) rot=(0,0,1;0rad)
  Support = -> [Pocket018]
  sketch-geometry (4):
    g0: LineSegment StartX=-48.5 StartY=61.5 StartZ=0 EndX=-40 EndY=61.5 EndZ=0
    g1: LineSegment StartX=-40 StartY=61.5 StartZ=0 EndX=-40 EndY=45 EndZ=0
    g2: LineSegment StartX=-40 StartY=45 StartZ=0 EndX=-48.5 EndY=45 EndZ=0
    g3: LineSegment StartX=-48.5 StartY=45 StartZ=0 EndX=-48.5 EndY=61.5 EndZ=0
  constraints (12):
    c: Coincident(g0,g1)
    c: Coincident(g1,g2)
    c: Coincident(g2,g3)
    c: Coincident(g3,g0)
    c: Horizontal(g0)
    c: Horizontal(g2)
    c: Vertical(g1)
    c: Vertical(g3)
    c: DistanceX(g0,g0) = 8.5
    c: DistanceY(g3,g3) = 16.5
    c: DistanceX(g1,g-1) = 40
    c: DistanceY(g-1,g2) = 45
FEATURE [PartDesign::Pocket] Pocket021  label="TimonePortaBatterie007"
  BaseFeature = -> Pocket018
  Length = 5
  Length2 = 100
  Profile = -> Sketch033
  Type = 0
FEATURE [PartDesign::Body] Body004  label="TimonePortaBatterie"
  Group = -> [Sketch023,Pad004,Sketch024,Pad005,Sketch025,Pad006,Sketch026,Pad007,Sketch027,Pocket018,Sketch033,Pocket021]
  Origin = -> Origin009
  Tip = -> Pocket021
FEATURE [App::Part] Part004  label="Timone Porta Batterie"
  Group = -> [Body004]
  Origin = -> Origin008
  Placement = pos=(0,25,-15) rot=(0,0,1;0rad)
